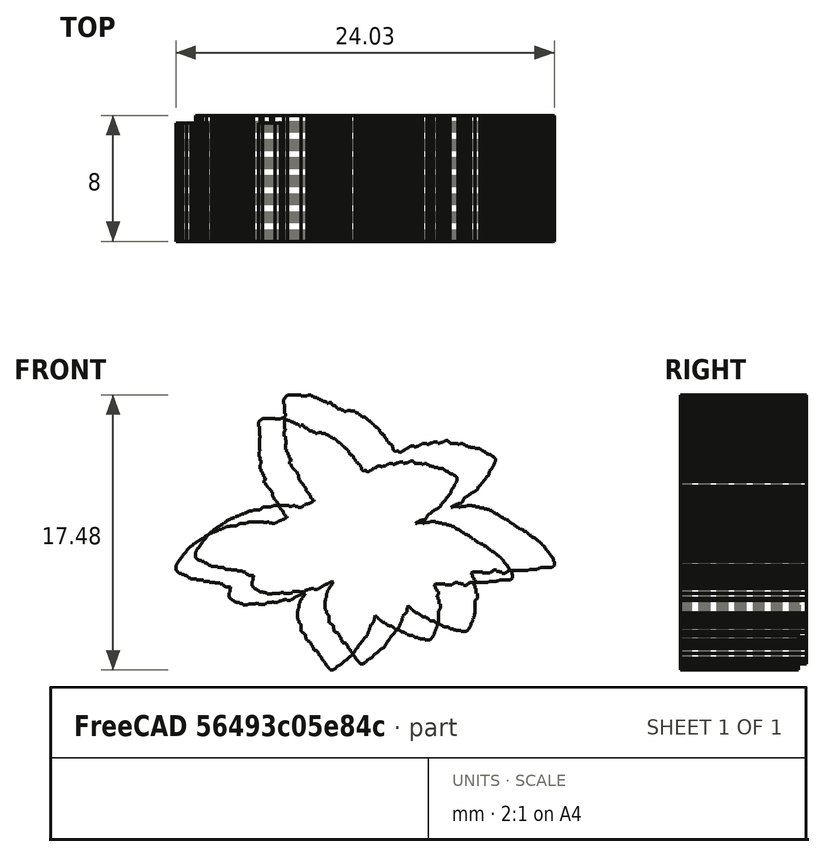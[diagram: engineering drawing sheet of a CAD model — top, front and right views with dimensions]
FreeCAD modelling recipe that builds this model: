
FCSTD DOCUMENT  (FreeCAD 0.20R29410 (Git))
Label: mintsLeafLogo_01_13_2023
License: All rights reserved
LicenseURL: http://en.wikipedia.org/wiki/All_rights_reserved
objects: Part::FeaturePython×2, Sketcher::SketchObject×1, Mesh::Feature×1, Part::Extrusion×1
note: 4 computed .brp shape members not serialized (recipe doc carries the construction recipe); baked Part::Feature solids carry a one-line shape summary decoded from their .brp

FEATURE [Sketcher::SketchObject] Sketch013
  FullyConstrained = false
  Placement = pos=(0,0,0) rot=(1,0,0;1.5708rad)
  sketch-geometry (884):
    g0: LineSegment StartX=35.7189 StartY=14.4677 StartZ=0 EndX=35.5415 EndY=14.2824 EndZ=0
    g1: LineSegment StartX=35.5415 StartY=14.2079 StartZ=0 EndX=35.4533 EndY=14.1342 EndZ=0
    g2: LineSegment StartX=35.4533 StartY=14.1342 StartZ=0 EndX=35.4583 EndY=14.0618 EndZ=0
    g3: LineSegment StartX=35.4583 StartY=14.0618 StartZ=0 EndX=35.3195 EndY=13.9216 EndZ=0
    g4: LineSegment StartX=35.3195 StartY=13.9216 StartZ=0 EndX=35.3195 EndY=13.853 EndZ=0
    g5: LineSegment StartX=35.3195 StartY=13.853 StartZ=0 EndX=35.248 EndY=13.7975 EndZ=0
    g6: LineSegment StartX=35.248 StartY=13.7975 StartZ=0 EndX=35.248 EndY=13.6573 EndZ=0
    g7: LineSegment StartX=35.248 StartY=13.6573 StartZ=0 EndX=35.1825 EndY=13.5912 EndZ=0
    g8: LineSegment StartX=35.1825 StartY=13.5912 StartZ=0 EndX=35.1825 EndY=13.2647 EndZ=0
    g9: LineSegment StartX=35.1825 StartY=13.2647 StartZ=0 EndX=35.0994 EndY=13.159 EndZ=0
    g10: LineSegment StartX=35.0994 StartY=13.159 StartZ=0 EndX=35.0994 EndY=13.0459 EndZ=0
    g11: LineSegment StartX=35.0994 StartY=13.0459 StartZ=0 EndX=35.0336 EndY=12.9565 EndZ=0
    g12: LineSegment StartX=35.0336 StartY=12.9565 StartZ=0 EndX=35.0336 EndY=12.3489 EndZ=0
    g13: LineSegment StartX=35.0336 StartY=12.3489 StartZ=0 EndX=35.1008 EndY=12.3489 EndZ=0
    g14: LineSegment StartX=35.1008 StartY=12.3489 StartZ=0 EndX=35.1008 EndY=12.2102 EndZ=0
    g15: LineSegment StartX=35.1008 StartY=12.2102 StartZ=0 EndX=35.1709 EndY=12.2072 EndZ=0
    g16: LineSegment StartX=35.1709 StartY=12.2072 StartZ=0 EndX=35.1709 EndY=11.9948 EndZ=0
    g17: LineSegment StartX=35.1709 StartY=11.9948 StartZ=0 EndX=35.2359 EndY=11.9948 EndZ=0
    g18: LineSegment StartX=35.2359 StartY=11.9948 StartZ=0 EndX=35.2359 EndY=11.9181 EndZ=0
    g19: LineSegment StartX=35.2359 StartY=11.9181 StartZ=0 EndX=35.3001 EndY=11.9181 EndZ=0
    g20: LineSegment StartX=35.3001 StartY=11.9181 StartZ=0 EndX=35.3001 EndY=11.8402 EndZ=0
    g21: LineSegment StartX=35.3001 StartY=11.8402 StartZ=0 EndX=35.3675 EndY=11.8402 EndZ=0
    g22: LineSegment StartX=35.3675 StartY=11.8402 StartZ=0 EndX=35.3675 EndY=11.2433 EndZ=0
    g23: LineSegment StartX=35.3675 StartY=11.2433 StartZ=0 EndX=35.435 EndY=11.2433 EndZ=0
    g24: LineSegment StartX=35.435 StartY=11.2433 StartZ=0 EndX=35.435 EndY=11.1727 EndZ=0
    g25: LineSegment StartX=35.435 StartY=11.1727 StartZ=0 EndX=35.5098 EndY=11.1727 EndZ=0
    g26: LineSegment StartX=35.5098 StartY=11.1727 StartZ=0 EndX=35.5098 EndY=11.1026 EndZ=0
    g27: LineSegment StartX=35.5098 StartY=11.1026 StartZ=0 EndX=35.6558 EndY=11.1026 EndZ=0
    g28: LineSegment StartX=35.6558 StartY=11.1026 StartZ=0 EndX=35.6558 EndY=11.0252 EndZ=0
    g29: LineSegment StartX=35.6558 StartY=11.0252 StartZ=0 EndX=35.7128 EndY=11.0252 EndZ=0
    g30: LineSegment StartX=35.7128 StartY=11.0252 StartZ=0 EndX=35.7128 EndY=10.7682 EndZ=0
    g31: LineSegment StartX=35.7128 StartY=10.7682 StartZ=0 EndX=35.7756 EndY=10.7681 EndZ=0
    g32: LineSegment StartX=35.7756 StartY=10.7681 StartZ=0 EndX=35.7756 EndY=10.5644 EndZ=0
    g33: LineSegment StartX=35.7756 StartY=10.5644 StartZ=0 EndX=35.846 EndY=10.5644 EndZ=0
    g34: LineSegment StartX=35.846 StartY=10.5644 StartZ=0 EndX=35.846 EndY=10.4767 EndZ=0
    g35: LineSegment StartX=35.846 StartY=10.4767 StartZ=0 EndX=35.988 EndY=10.4767 EndZ=0
    g36: LineSegment StartX=35.988 StartY=10.4767 StartZ=0 EndX=35.988 EndY=10.4228 EndZ=0
    g37: LineSegment StartX=35.988 StartY=10.4228 StartZ=0 EndX=36.1201 EndY=10.4228 EndZ=0
    g38: LineSegment StartX=36.1201 StartY=10.4228 StartZ=0 EndX=36.1201 EndY=10.2907 EndZ=0
    g39: LineSegment StartX=36.1201 StartY=10.2907 StartZ=0 EndX=36.1926 EndY=10.2907 EndZ=0
    g40: LineSegment StartX=36.1926 StartY=10.2907 StartZ=0 EndX=36.1926 EndY=10.1585 EndZ=0
    g41: LineSegment StartX=36.1926 StartY=10.1585 StartZ=0 EndX=36.2533 EndY=10.1585 EndZ=0
    g42: LineSegment StartX=36.2533 StartY=10.1585 StartZ=0 EndX=36.2533 EndY=10.0897 EndZ=0
    g43: LineSegment StartX=36.2533 StartY=10.0897 StartZ=0 EndX=36.3179 EndY=10.0897 EndZ=0
    g44: LineSegment StartX=36.3179 StartY=10.0897 StartZ=0 EndX=36.3179 EndY=9.8871 EndZ=0
    g45: LineSegment StartX=36.3179 StartY=9.8871 StartZ=0 EndX=36.3888 EndY=9.8871 EndZ=0
    g46: LineSegment StartX=36.3888 StartY=9.8871 StartZ=0 EndX=36.3888 EndY=9.73503 EndZ=0
    g47: LineSegment StartX=36.3888 StartY=9.73503 StartZ=0 EndX=36.4516 EndY=9.73503 EndZ=0
    g48: LineSegment StartX=36.4516 StartY=9.73503 StartZ=0 EndX=36.4516 EndY=9.65617 EndZ=0
    g49: LineSegment StartX=36.4516 StartY=9.65617 StartZ=0 EndX=36.6707 EndY=9.65617 EndZ=0
    g50: LineSegment StartX=36.6707 StartY=9.65617 StartZ=0 EndX=36.6707 EndY=9.58899 EndZ=0
    g51: LineSegment StartX=36.6707 StartY=9.58899 StartZ=0 EndX=36.7335 EndY=9.58899 EndZ=0
    g52: LineSegment StartX=36.7335 StartY=9.58899 StartZ=0 EndX=36.7335 EndY=9.51158 EndZ=0
    g53: LineSegment StartX=36.7335 StartY=9.51158 StartZ=0 EndX=36.7948 EndY=9.51158 EndZ=0
    g54: LineSegment StartX=36.7948 StartY=9.51158 StartZ=0 EndX=36.7948 EndY=9.40351 EndZ=0
    g55: LineSegment StartX=36.7948 StartY=9.40351 StartZ=0 EndX=36.8664 EndY=9.40351 EndZ=0
    g56: LineSegment StartX=36.8664 StartY=9.40351 StartZ=0 EndX=36.8664 EndY=9.2487 EndZ=0
    g57: LineSegment StartX=36.8664 StartY=9.2487 StartZ=0 EndX=36.9292 EndY=9.2487 EndZ=0
    g58: LineSegment StartX=36.9292 StartY=9.2487 StartZ=0 EndX=36.9292 EndY=9.18298 EndZ=0
    g59: LineSegment StartX=36.9292 StartY=9.18298 StartZ=0 EndX=37.0036 EndY=9.18298 EndZ=0
    g60: LineSegment StartX=37.0036 StartY=9.18298 StartZ=0 EndX=37.0036 EndY=9.12121 EndZ=0
    g61: LineSegment StartX=37.0036 StartY=9.12121 StartZ=0 EndX=37.066 EndY=9.12121 EndZ=0
    g62: LineSegment StartX=37.066 StartY=9.12121 StartZ=0 EndX=37.066 EndY=8.98122 EndZ=0
    g63: LineSegment StartX=37.066 StartY=8.98122 StartZ=0 EndX=37.1365 EndY=8.98122 EndZ=0
    g64: LineSegment StartX=37.1365 StartY=8.98122 StartZ=0 EndX=37.1365 EndY=8.85617 EndZ=0
    g65: LineSegment StartX=37.1365 StartY=8.85617 StartZ=0 EndX=37.2117 EndY=8.85617 EndZ=0
    g66: LineSegment StartX=37.2117 StartY=8.85617 StartZ=0 EndX=37.2117 EndY=8.77808 EndZ=0
    g67: LineSegment StartX=37.2117 StartY=8.77808 StartZ=0 EndX=37.276 EndY=8.7779 EndZ=0
    g68: LineSegment StartX=37.276 StartY=8.7779 StartZ=0 EndX=37.276 EndY=8.70839 EndZ=0
    g69: LineSegment StartX=37.276 StartY=8.70839 StartZ=0 EndX=37.3475 EndY=8.70839 EndZ=0
    g70: LineSegment StartX=37.3475 StartY=8.70839 StartZ=0 EndX=37.3475 EndY=8.58602 EndZ=0
    g71: LineSegment StartX=37.3475 StartY=8.58602 StartZ=0 EndX=37.4111 EndY=8.58602 EndZ=0
    g72: LineSegment StartX=37.4111 StartY=8.58602 StartZ=0 EndX=37.4111 EndY=8.50272 EndZ=0
    g73: LineSegment StartX=37.4111 StartY=8.50272 StartZ=0 EndX=37.4778 EndY=8.50272 EndZ=0
    g74: LineSegment StartX=37.4778 StartY=8.50272 StartZ=0 EndX=37.4778 EndY=8.37852 EndZ=0
    g75: LineSegment StartX=37.4778 StartY=8.37852 StartZ=0 EndX=37.55 EndY=8.37852 EndZ=0
    g76: LineSegment StartX=37.55 StartY=8.37852 StartZ=0 EndX=37.55 EndY=8.29594 EndZ=0
    g77: LineSegment StartX=37.55 StartY=8.29594 StartZ=0 EndX=37.6238 EndY=8.29594 EndZ=0
    g78: LineSegment StartX=37.6238 StartY=8.29594 StartZ=0 EndX=37.6238 EndY=8.20831 EndZ=0
    g79: LineSegment StartX=37.6238 StartY=8.20831 StartZ=0 EndX=37.6953 EndY=8.21123 EndZ=0
    g80: LineSegment StartX=37.6953 StartY=8.21123 StartZ=0 EndX=37.6953 EndY=8.14022 EndZ=0
    g81: LineSegment StartX=37.6953 StartY=8.14022 StartZ=0 EndX=37.7536 EndY=8.14414 EndZ=0
    g82: LineSegment StartX=37.7536 StartY=8.14414 StartZ=0 EndX=37.7574 EndY=8.06459 EndZ=0
    g83: LineSegment StartX=37.7574 StartY=8.06459 StartZ=0 EndX=37.8181 EndY=8.06459 EndZ=0
    g84: LineSegment StartX=37.8181 StartY=8.06459 StartZ=0 EndX=37.8216 EndY=7.98967 EndZ=0
    g85: LineSegment StartX=37.8216 StartY=7.98967 StartZ=0 EndX=38.1025 EndY=7.98967 EndZ=0
    g86: LineSegment StartX=38.1025 StartY=7.98967 StartZ=0 EndX=38.1917 EndY=8.08042 EndZ=0
    g87: LineSegment StartX=38.1917 StartY=8.08042 StartZ=0 EndX=38.2417 EndY=8.08577 EndZ=0
    g88: LineSegment StartX=38.2417 StartY=8.08577 StartZ=0 EndX=38.4557 EndY=8.32302 EndZ=0
    g89: LineSegment StartX=38.4557 StartY=8.32302 StartZ=0 EndX=38.5235 EndY=8.32302 EndZ=0
    g90: LineSegment StartX=38.5235 StartY=8.32302 StartZ=0 EndX=38.5887 EndY=8.40314 EndZ=0
    g91: LineSegment StartX=38.5887 StartY=8.40314 StartZ=0 EndX=38.6773 EndY=8.40314 EndZ=0
    g92: LineSegment StartX=38.6773 StartY=8.40314 StartZ=0 EndX=39.0643 EndY=8.80818 EndZ=0
    g93: LineSegment StartX=39.0643 StartY=8.80818 StartZ=0 EndX=39.152 EndY=8.80818 EndZ=0
    g94: LineSegment StartX=39.152 StartY=8.80818 StartZ=0 EndX=39.5355 EndY=9.19803 EndZ=0
    g95: LineSegment StartX=39.5355 StartY=9.19803 StartZ=0 EndX=39.6318 EndY=9.19803 EndZ=0
    g96: LineSegment StartX=39.6318 StartY=9.19803 StartZ=0 EndX=39.792 EndY=9.38195 EndZ=0
    g97: LineSegment StartX=39.792 StartY=9.38195 StartZ=0 EndX=39.7884 EndY=9.45608 EndZ=0
    g98: LineSegment StartX=39.7884 StartY=9.45608 StartZ=0 EndX=39.9772 EndY=9.63446 EndZ=0
    g99: LineSegment StartX=39.9772 StartY=9.63446 StartZ=0 EndX=39.9772 EndY=9.72533 EndZ=0
    g100: LineSegment StartX=39.9772 StartY=9.72533 StartZ=0 EndX=40.1697 EndY=9.91904 EndZ=0
    g101: LineSegment StartX=40.1697 StartY=9.91904 StartZ=0 EndX=40.1746 EndY=9.99558 EndZ=0
    g102: LineSegment StartX=40.1746 StartY=9.99558 StartZ=0 EndX=40.2388 EndY=10.0603 EndZ=0
    g103: LineSegment StartX=40.2388 StartY=10.0603 StartZ=0 EndX=40.2423 EndY=10.1261 EndZ=0
    g104: LineSegment StartX=40.2423 StartY=10.1261 StartZ=0 EndX=40.5948 EndY=10.4793 EndZ=0
    g105: LineSegment StartX=40.5948 StartY=10.4793 StartZ=0 EndX=40.5948 EndY=10.5499 EndZ=0
    g106: LineSegment StartX=40.5948 StartY=10.5499 StartZ=0 EndX=40.6701 EndY=10.618 EndZ=0
    g107: LineSegment StartX=40.6701 StartY=10.618 StartZ=0 EndX=40.6581 EndY=10.6527 EndZ=0
    g108: LineSegment StartX=40.6581 StartY=10.6527 StartZ=0 EndX=40.6988 EndY=10.6527 EndZ=0
    g109: LineSegment StartX=40.6988 StartY=10.6527 StartZ=0 EndX=40.9317 EndY=10.8877 EndZ=0
    g110: LineSegment StartX=40.9317 StartY=10.8877 StartZ=0 EndX=40.9317 EndY=10.9592 EndZ=0
    g111: LineSegment StartX=40.9317 StartY=10.9592 StartZ=0 EndX=41.0136 EndY=11.0405 EndZ=0
    g112: LineSegment StartX=41.0136 StartY=11.0405 StartZ=0 EndX=41.0068 EndY=11.1648 EndZ=0
    g113: LineSegment StartX=41.0068 StartY=11.1648 StartZ=0 EndX=41.0763 EndY=11.2275 EndZ=0
    g114: LineSegment StartX=41.0763 StartY=11.2275 StartZ=0 EndX=41.0723 EndY=11.2979 EndZ=0
    g115: LineSegment StartX=41.0723 StartY=11.2979 StartZ=0 EndX=41.15 EndY=11.3821 EndZ=0
    g116: LineSegment StartX=41.15 StartY=11.3821 StartZ=0 EndX=41.15 EndY=11.5724 EndZ=0
    g117: LineSegment StartX=41.15 StartY=11.5724 StartZ=0 EndX=41.2317 EndY=11.6351 EndZ=0
    g118: LineSegment StartX=41.2317 StartY=11.6351 StartZ=0 EndX=41.2155 EndY=11.7717 EndZ=0
    g119: LineSegment StartX=41.2155 StartY=11.7717 StartZ=0 EndX=41.2837 EndY=11.8432 EndZ=0
    g120: LineSegment StartX=41.2837 StartY=11.8432 StartZ=0 EndX=41.2786 EndY=11.8698 EndZ=0
    g121: LineSegment StartX=41.2786 StartY=11.8698 StartZ=0 EndX=41.3138 EndY=11.8698 EndZ=0
    g122: LineSegment StartX=41.3138 StartY=11.8698 StartZ=0 EndX=41.5455 EndY=12.1045 EndZ=0
    g123: LineSegment StartX=41.5455 StartY=12.1045 StartZ=0 EndX=41.5618 EndY=12.4305 EndZ=0
    g124: LineSegment StartX=41.5618 StartY=12.4305 StartZ=0 EndX=41.6277 EndY=12.505 EndZ=0
    g125: LineSegment StartX=41.6277 StartY=12.505 StartZ=0 EndX=41.6277 EndY=12.6108 EndZ=0
    g126: LineSegment StartX=41.6277 StartY=12.6108 StartZ=0 EndX=41.692 EndY=12.5393 EndZ=0
    g127: LineSegment StartX=41.692 StartY=12.5393 StartZ=0 EndX=41.7679 EndY=12.5393 EndZ=0
    g128: LineSegment StartX=41.7679 StartY=12.5393 StartZ=0 EndX=41.7679 EndY=12.4516 EndZ=0
    g129: LineSegment StartX=41.7679 StartY=12.4516 StartZ=0 EndX=41.8336 EndY=12.4546 EndZ=0
    g130: LineSegment StartX=41.8336 StartY=12.4546 StartZ=0 EndX=41.8336 EndY=12.3903 EndZ=0
    g131: LineSegment StartX=41.8336 StartY=12.3903 StartZ=0 EndX=41.8935 EndY=12.3903 EndZ=0
    g132: LineSegment StartX=41.8935 StartY=12.3903 StartZ=0 EndX=41.8935 EndY=12.3173 EndZ=0
    g133: LineSegment StartX=41.8935 StartY=12.3173 StartZ=0 EndX=41.9592 EndY=12.3217 EndZ=0
    g134: LineSegment StartX=41.9592 StartY=12.3217 StartZ=0 EndX=41.9651 EndY=12.2501 EndZ=0
    g135: LineSegment StartX=41.9651 StartY=12.2501 StartZ=0 EndX=42.0235 EndY=12.2559 EndZ=0
    g136: LineSegment StartX=42.0235 StartY=12.2559 StartZ=0 EndX=42.0264 EndY=12.1829 EndZ=0
    g137: LineSegment StartX=42.0264 StartY=12.1829 StartZ=0 EndX=42.1067 EndY=12.1888 EndZ=0
    g138: LineSegment StartX=42.1067 StartY=12.1888 StartZ=0 EndX=42.1067 EndY=12.1143 EndZ=0
    g139: LineSegment StartX=42.1067 StartY=12.1143 StartZ=0 EndX=42.2426 EndY=12.1216 EndZ=0
    g140: LineSegment StartX=42.2426 StartY=12.1216 StartZ=0 EndX=42.2426 EndY=12.0413 EndZ=0
    g141: LineSegment StartX=42.2426 StartY=12.0413 StartZ=0 EndX=42.4427 EndY=12.0413 EndZ=0
    g142: LineSegment StartX=42.4427 StartY=12.0413 StartZ=0 EndX=42.45 EndY=11.9566 EndZ=0
    g143: LineSegment StartX=42.45 StartY=11.9566 StartZ=0 EndX=42.523 EndY=11.9639 EndZ=0
    g144: LineSegment StartX=42.523 StartY=11.9639 StartZ=0 EndX=42.5274 EndY=11.8952 EndZ=0
    g145: LineSegment StartX=42.5274 StartY=11.8952 StartZ=0 EndX=42.5931 EndY=11.9011 EndZ=0
    g146: LineSegment StartX=42.5931 StartY=11.9011 StartZ=0 EndX=42.5931 EndY=11.847 EndZ=0
    g147: LineSegment StartX=42.5931 StartY=11.847 StartZ=0 EndX=42.6457 EndY=11.8499 EndZ=0
    g148: LineSegment StartX=42.6457 StartY=11.8499 StartZ=0 EndX=42.6457 EndY=11.7886 EndZ=0
    g149: LineSegment StartX=42.6457 StartY=11.7886 StartZ=0 EndX=42.7844 EndY=11.7886 EndZ=0
    g150: LineSegment StartX=42.7844 StartY=11.7886 StartZ=0 EndX=42.7844 EndY=11.7131 EndZ=0
    g151: LineSegment StartX=42.7844 StartY=11.7131 StartZ=0 EndX=43.0642 EndY=11.7131 EndZ=0
    g152: LineSegment StartX=43.0642 StartY=11.7131 StartZ=0 EndX=43.0642 EndY=11.6357 EndZ=0
    g153: LineSegment StartX=43.0642 StartY=11.6357 StartZ=0 EndX=43.1985 EndY=11.6357 EndZ=0
    g154: LineSegment StartX=43.1985 StartY=11.6357 StartZ=0 EndX=43.1985 EndY=11.5714 EndZ=0
    g155: LineSegment StartX=43.1985 StartY=11.5714 StartZ=0 EndX=43.2613 EndY=11.5714 EndZ=0
    g156: LineSegment StartX=43.2613 StartY=11.5714 StartZ=0 EndX=43.2613 EndY=11.5086 EndZ=0
    g157: LineSegment StartX=43.2613 StartY=11.5086 StartZ=0 EndX=43.3285 EndY=11.5086 EndZ=0
    g158: LineSegment StartX=43.3285 StartY=11.5086 StartZ=0 EndX=43.3285 EndY=11.4327 EndZ=0
    g159: LineSegment StartX=43.3285 StartY=11.4327 StartZ=0 EndX=43.3913 EndY=11.4371 EndZ=0
    g160: LineSegment StartX=43.3913 StartY=11.4371 StartZ=0 EndX=43.3932 EndY=11.3717 EndZ=0
    g161: LineSegment StartX=43.3932 StartY=11.3717 StartZ=0 EndX=43.7436 EndY=11.3717 EndZ=0
    g162: LineSegment StartX=43.7436 StartY=11.3717 StartZ=0 EndX=43.7436 EndY=11.3021 EndZ=0
    g163: LineSegment StartX=43.7436 StartY=11.3021 StartZ=0 EndX=43.8098 EndY=11.3021 EndZ=0
    g164: LineSegment StartX=43.8098 StartY=11.3021 StartZ=0 EndX=43.8134 EndY=11.2285 EndZ=0
    g165: LineSegment StartX=43.8134 StartY=11.2285 StartZ=0 EndX=44.0238 EndY=11.2285 EndZ=0
    g166: LineSegment StartX=44.0238 StartY=11.2285 StartZ=0 EndX=44.0238 EndY=11.1603 EndZ=0
    g167: LineSegment StartX=44.0238 StartY=11.1603 StartZ=0 EndX=44.1542 EndY=11.1603 EndZ=0
    g168: LineSegment StartX=44.1542 StartY=11.1603 StartZ=0 EndX=44.1506 EndY=11.0922 EndZ=0
    g169: LineSegment StartX=44.1506 StartY=11.0922 StartZ=0 EndX=44.2845 EndY=11.1005 EndZ=0
    g170: LineSegment StartX=44.2845 StartY=11.1005 StartZ=0 EndX=44.2845 EndY=11.0276 EndZ=0
    g171: LineSegment StartX=44.2845 StartY=11.0276 StartZ=0 EndX=44.3538 EndY=11.0312 EndZ=0
    g172: LineSegment StartX=44.3538 StartY=11.0312 StartZ=0 EndX=44.3538 EndY=10.9534 EndZ=0
    g173: LineSegment StartX=44.3538 StartY=10.9534 StartZ=0 EndX=44.4925 EndY=10.9534 EndZ=0
    g174: LineSegment StartX=44.4925 StartY=10.9534 StartZ=0 EndX=44.4925 EndY=10.9066 EndZ=0
    g175: LineSegment StartX=44.4925 StartY=10.9066 StartZ=0 EndX=44.8405 EndY=10.9066 EndZ=0
    g176: LineSegment StartX=44.8405 StartY=10.9066 StartZ=0 EndX=44.8405 EndY=10.8227 EndZ=0
    g177: LineSegment StartX=44.8405 StartY=10.8227 StartZ=0 EndX=44.9671 EndY=10.8245 EndZ=0
    g178: LineSegment StartX=44.9671 StartY=10.8245 StartZ=0 EndX=44.9671 EndY=10.7496 EndZ=0
    g179: LineSegment StartX=44.9671 StartY=10.7496 StartZ=0 EndX=45.2382 EndY=10.7496 EndZ=0
    g180: LineSegment StartX=45.2382 StartY=10.7496 StartZ=0 EndX=45.2382 EndY=10.6783 EndZ=0
    g181: LineSegment StartX=45.2382 StartY=10.6783 StartZ=0 EndX=45.438 EndY=10.6783 EndZ=0
    g182: LineSegment StartX=45.438 StartY=10.6783 StartZ=0 EndX=45.438 EndY=10.6176 EndZ=0
    g183: LineSegment StartX=45.438 StartY=10.6176 StartZ=0 EndX=45.8572 EndY=10.6176 EndZ=0
    g184: LineSegment StartX=45.8572 StartY=10.6176 StartZ=0 EndX=45.8572 EndY=10.548 EndZ=0
    g185: LineSegment StartX=45.8572 StartY=10.548 StartZ=0 EndX=46.2711 EndY=10.548 EndZ=0
    g186: LineSegment StartX=46.2711 StartY=10.548 StartZ=0 EndX=46.5712 EndY=10.876 EndZ=0
    g187: LineSegment StartX=46.5712 StartY=10.876 StartZ=0 EndX=46.568 EndY=10.9537 EndZ=0
    g188: LineSegment StartX=46.568 StartY=10.9537 StartZ=0 EndX=46.6513 EndY=11.0387 EndZ=0
    g189: LineSegment StartX=46.6513 StartY=11.0387 StartZ=0 EndX=46.6513 EndY=11.2162 EndZ=0
    g190: LineSegment StartX=46.6513 StartY=11.2162 StartZ=0 EndX=46.7535 EndY=11.317 EndZ=0
    g191: LineSegment StartX=46.7535 StartY=11.317 StartZ=0 EndX=46.7462 EndY=11.4353 EndZ=0
    g192: LineSegment StartX=46.7462 StartY=11.4353 StartZ=0 EndX=46.8178 EndY=11.5141 EndZ=0
    g193: LineSegment StartX=46.8178 StartY=11.5141 StartZ=0 EndX=46.8081 EndY=11.636 EndZ=0
    g194: LineSegment StartX=46.8081 StartY=11.636 StartZ=0 EndX=46.8919 EndY=11.7287 EndZ=0
    g195: LineSegment StartX=46.8919 StartY=11.7287 StartZ=0 EndX=46.8919 EndY=11.9142 EndZ=0
    g196: LineSegment StartX=46.8919 StartY=11.9142 StartZ=0 EndX=46.9704 EndY=12.0106 EndZ=0
    g197: LineSegment StartX=46.9704 StartY=12.0106 StartZ=0 EndX=46.9704 EndY=13.0147 EndZ=0
    g198: LineSegment StartX=46.9704 StartY=13.0147 StartZ=0 EndX=47.1435 EndY=13.1957 EndZ=0
    g199: LineSegment StartX=47.1435 StartY=13.1957 StartZ=0 EndX=47.1435 EndY=13.5812 EndZ=0
    g200: LineSegment StartX=47.1435 StartY=13.5812 StartZ=0 EndX=47.0232 EndY=13.5812 EndZ=0
    g201: LineSegment StartX=47.0232 StartY=13.5812 StartZ=0 EndX=47.0232 EndY=13.968 EndZ=0
    g202: LineSegment StartX=47.0232 StartY=13.968 StartZ=0 EndX=46.9387 EndY=13.981 EndZ=0
    g203: LineSegment StartX=46.9387 StartY=13.981 StartZ=0 EndX=46.9387 EndY=14.1923 EndZ=0
    g204: LineSegment StartX=46.9387 StartY=14.1923 StartZ=0 EndX=46.8607 EndY=14.189 EndZ=0
    g205: LineSegment StartX=46.8607 StartY=14.189 StartZ=0 EndX=46.8607 EndY=14.2768 EndZ=0
    g206: LineSegment StartX=46.8607 StartY=14.2768 StartZ=0 EndX=46.9745 EndY=14.4003 EndZ=0
    g207: LineSegment StartX=46.9745 StartY=14.4003 StartZ=0 EndX=46.9842 EndY=14.6473 EndZ=0
    g208: LineSegment StartX=46.9842 StartY=14.6473 StartZ=0 EndX=46.8672 EndY=14.6603 EndZ=0
    g209: LineSegment StartX=46.8672 StartY=14.6603 StartZ=0 EndX=46.8672 EndY=14.8066 EndZ=0
    g210: LineSegment StartX=46.8672 StartY=14.8066 StartZ=0 EndX=46.799 EndY=14.8131 EndZ=0
    g211: LineSegment StartX=46.799 StartY=14.8131 StartZ=0 EndX=46.7957 EndY=14.8846 EndZ=0
    g212: LineSegment StartX=46.7957 StartY=14.8846 StartZ=0 EndX=46.7372 EndY=14.8911 EndZ=0
    g213: LineSegment StartX=46.7372 StartY=14.8911 StartZ=0 EndX=46.7502 EndY=15.0699 EndZ=0
    g214: LineSegment StartX=46.7502 StartY=15.0699 StartZ=0 EndX=46.6592 EndY=15.0764 EndZ=0
    g215: LineSegment StartX=46.6592 StartY=15.0764 StartZ=0 EndX=46.6592 EndY=15.2096 EndZ=0
    g216: LineSegment StartX=46.6592 StartY=15.2096 StartZ=0 EndX=46.7535 EndY=15.2811 EndZ=0
    g217: LineSegment StartX=46.7535 StartY=15.2811 StartZ=0 EndX=47.5498 EndY=15.2811 EndZ=0
    g218: LineSegment StartX=47.5498 StartY=15.2811 StartZ=0 EndX=47.5498 EndY=15.2015 EndZ=0
    g219: LineSegment StartX=47.5498 StartY=15.2015 StartZ=0 EndX=48.1326 EndY=15.2015 EndZ=0
    g220: LineSegment StartX=48.1326 StartY=15.2015 StartZ=0 EndX=48.1915 EndY=15.2887 EndZ=0
    g221: LineSegment StartX=48.1915 StartY=15.2887 StartZ=0 EndX=48.2811 EndY=15.2887 EndZ=0
    g222: LineSegment StartX=48.2811 StartY=15.2887 StartZ=0 EndX=48.4046 EndY=15.4194 EndZ=0
    g223: LineSegment StartX=48.4046 StartY=15.4194 StartZ=0 EndX=48.6512 EndY=15.4194 EndZ=0
    g224: LineSegment StartX=48.6512 StartY=15.4194 StartZ=0 EndX=48.6512 EndY=15.3322 EndZ=0
    g225: LineSegment StartX=48.6512 StartY=15.3322 StartZ=0 EndX=48.9084 EndY=15.3322 EndZ=0
    g226: LineSegment StartX=48.9084 StartY=15.3322 StartZ=0 EndX=48.9084 EndY=15.2647 EndZ=0
    g227: LineSegment StartX=48.9084 StartY=15.2647 StartZ=0 EndX=49.1131 EndY=15.2647 EndZ=0
    g228: LineSegment StartX=49.1131 StartY=15.2647 StartZ=0 EndX=49.1131 EndY=15.171 EndZ=0
    g229: LineSegment StartX=49.1131 StartY=15.171 StartZ=0 EndX=49.344 EndY=15.171 EndZ=0
    g230: LineSegment StartX=49.344 StartY=15.171 StartZ=0 EndX=49.4317 EndY=15.2779 EndZ=0
    g231: LineSegment StartX=49.4317 StartY=15.2779 StartZ=0 EndX=49.513 EndY=15.2714 EndZ=0
    g232: LineSegment StartX=49.513 StartY=15.2714 StartZ=0 EndX=49.6365 EndY=15.4177 EndZ=0
    g233: LineSegment StartX=49.6365 StartY=15.4177 StartZ=0 EndX=51.1609 EndY=15.4177 EndZ=0
    g234: LineSegment StartX=51.1609 StartY=15.4177 StartZ=0 EndX=51.2713 EndY=15.4747 EndZ=0
    g235: LineSegment StartX=51.2713 StartY=15.4747 StartZ=0 EndX=51.8707 EndY=15.4747 EndZ=0
    g236: LineSegment StartX=51.8707 StartY=15.4747 StartZ=0 EndX=51.9501 EndY=15.5501 EndZ=0
    g237: LineSegment StartX=51.9501 StartY=15.5501 StartZ=0 EndX=52.0613 EndY=15.5501 EndZ=0
    g238: LineSegment StartX=52.0613 StartY=15.5501 StartZ=0 EndX=52.1566 EndY=15.6335 EndZ=0
    g239: LineSegment StartX=52.1566 StartY=15.6335 StartZ=0 EndX=53.0776 EndY=15.6335 EndZ=0
    g240: LineSegment StartX=53.0776 StartY=15.6335 StartZ=0 EndX=53.2557 EndY=15.8082 EndZ=0
    g241: LineSegment StartX=53.2557 StartY=15.8082 StartZ=0 EndX=53.2557 EndY=16.103 EndZ=0
    g242: LineSegment StartX=53.2557 StartY=16.103 StartZ=0 EndX=53.1958 EndY=16.103 EndZ=0
    g243: LineSegment StartX=53.1958 StartY=16.103 StartZ=0 EndX=53.1958 EndY=16.3046 EndZ=0
    g244: LineSegment StartX=53.1958 StartY=16.3046 StartZ=0 EndX=53.1301 EndY=16.3017 EndZ=0
    g245: LineSegment StartX=53.1301 StartY=16.3017 StartZ=0 EndX=53.1301 EndY=16.4404 EndZ=0
    g246: LineSegment StartX=53.1301 StartY=16.4404 StartZ=0 EndX=53.0594 EndY=16.4404 EndZ=0
    g247: LineSegment StartX=53.0594 StartY=16.4404 StartZ=0 EndX=53.0558 EndY=16.5171 EndZ=0
    g248: LineSegment StartX=53.0558 StartY=16.5171 StartZ=0 EndX=52.9773 EndY=16.5171 EndZ=0
    g249: LineSegment StartX=52.9773 StartY=16.5171 StartZ=0 EndX=52.9773 EndY=16.6455 EndZ=0
    g250: LineSegment StartX=52.9773 StartY=16.6455 StartZ=0 EndX=52.9219 EndY=16.6452 EndZ=0
    g251: LineSegment StartX=52.9219 StartY=16.6452 StartZ=0 EndX=52.9219 EndY=16.7146 EndZ=0
    g252: LineSegment StartX=52.9219 StartY=16.7146 StartZ=0 EndX=52.8549 EndY=16.7146 EndZ=0
    g253: LineSegment StartX=52.8549 StartY=16.7146 StartZ=0 EndX=52.8535 EndY=16.7863 EndZ=0
    g254: LineSegment StartX=52.8535 StartY=16.7863 StartZ=0 EndX=52.7868 EndY=16.7863 EndZ=0
    g255: LineSegment StartX=52.7868 StartY=16.7863 StartZ=0 EndX=52.7868 EndY=16.9211 EndZ=0
    g256: LineSegment StartX=52.7868 StartY=16.9211 StartZ=0 EndX=52.715 EndY=16.9211 EndZ=0
    g257: LineSegment StartX=52.715 StartY=16.9211 StartZ=0 EndX=52.715 EndY=16.98 EndZ=0
    g258: LineSegment StartX=52.715 StartY=16.98 StartZ=0 EndX=52.6457 EndY=16.98 EndZ=0
    g259: LineSegment StartX=52.6457 StartY=16.98 StartZ=0 EndX=52.6457 EndY=17.0366 EndZ=0
    g260: LineSegment StartX=52.6457 StartY=17.0366 StartZ=0 EndX=52.5763 EndY=17.0366 EndZ=0
    g261: LineSegment StartX=52.5763 StartY=17.0366 StartZ=0 EndX=52.5763 EndY=17.128 EndZ=0
    g262: LineSegment StartX=52.5763 StartY=17.128 StartZ=0 EndX=52.5147 EndY=17.128 EndZ=0
    g263: LineSegment StartX=52.5147 StartY=17.128 StartZ=0 EndX=52.5147 EndY=17.2695 EndZ=0
    g264: LineSegment StartX=52.5147 StartY=17.2695 StartZ=0 EndX=52.4502 EndY=17.2647 EndZ=0
    g265: LineSegment StartX=52.4502 StartY=17.2647 StartZ=0 EndX=52.4454 EndY=17.336 EndZ=0
    g266: LineSegment StartX=52.4454 StartY=17.336 StartZ=0 EndX=52.3797 EndY=17.3384 EndZ=0
    g267: LineSegment StartX=52.3797 StartY=17.3384 StartZ=0 EndX=52.3829 EndY=17.4058 EndZ=0
    g268: LineSegment StartX=52.3829 StartY=17.4058 StartZ=0 EndX=52.318 EndY=17.4026 EndZ=0
    g269: LineSegment StartX=52.318 StartY=17.4026 StartZ=0 EndX=52.318 EndY=17.4715 EndZ=0
    g270: LineSegment StartX=52.318 StartY=17.4715 StartZ=0 EndX=52.2451 EndY=17.4715 EndZ=0
    g271: LineSegment StartX=52.2451 StartY=17.4715 StartZ=0 EndX=52.2451 EndY=17.5364 EndZ=0
    g272: LineSegment StartX=52.2451 StartY=17.5364 StartZ=0 EndX=52.1833 EndY=17.5388 EndZ=0
    g273: LineSegment StartX=52.1833 StartY=17.5388 StartZ=0 EndX=52.1833 EndY=17.6077 EndZ=0
    g274: LineSegment StartX=52.1833 StartY=17.6077 StartZ=0 EndX=52.1144 EndY=17.6077 EndZ=0
    g275: LineSegment StartX=52.1144 StartY=17.6077 StartZ=0 EndX=52.1144 EndY=17.6741 EndZ=0
    g276: LineSegment StartX=52.1144 StartY=17.6741 StartZ=0 EndX=52.0495 EndY=17.6741 EndZ=0
    g277: LineSegment StartX=52.0495 StartY=17.6741 StartZ=0 EndX=52.0495 EndY=17.7495 EndZ=0
    g278: LineSegment StartX=52.0495 StartY=17.7495 StartZ=0 EndX=51.9017 EndY=17.7495 EndZ=0
    g279: LineSegment StartX=51.9017 StartY=17.7495 StartZ=0 EndX=51.9017 EndY=17.8092 EndZ=0
    g280: LineSegment StartX=51.9017 StartY=17.8092 StartZ=0 EndX=51.8351 EndY=17.8092 EndZ=0
    g281: LineSegment StartX=51.8351 StartY=17.8092 StartZ=0 EndX=51.8351 EndY=17.8911 EndZ=0
    g282: LineSegment StartX=51.8351 StartY=17.8911 StartZ=0 EndX=51.7639 EndY=17.8911 EndZ=0
    g283: LineSegment StartX=51.7639 StartY=17.8911 StartZ=0 EndX=51.7639 EndY=17.9626 EndZ=0
    g284: LineSegment StartX=51.7639 StartY=17.9626 StartZ=0 EndX=51.6325 EndY=17.9626 EndZ=0
    g285: LineSegment StartX=51.6325 StartY=17.9626 StartZ=0 EndX=51.6325 EndY=18.0284 EndZ=0
    g286: LineSegment StartX=51.6325 StartY=18.0284 StartZ=0 EndX=51.485 EndY=18.0284 EndZ=0
    g287: LineSegment StartX=51.485 StartY=18.0284 StartZ=0 EndX=51.485 EndY=18.0711 EndZ=0
    g288: LineSegment StartX=51.485 StartY=18.0711 StartZ=0 EndX=51.4163 EndY=18.0711 EndZ=0
    g289: LineSegment StartX=51.4163 StartY=18.0711 StartZ=0 EndX=51.4163 EndY=18.1587 EndZ=0
    g290: LineSegment StartX=51.4163 StartY=18.1587 StartZ=0 EndX=51.2878 EndY=18.1587 EndZ=0
    g291: LineSegment StartX=51.2878 StartY=18.1587 StartZ=0 EndX=51.2878 EndY=18.2275 EndZ=0
    g292: LineSegment StartX=51.2878 StartY=18.2275 StartZ=0 EndX=51.2232 EndY=18.2275 EndZ=0
    g293: LineSegment StartX=51.2232 StartY=18.2275 StartZ=0 EndX=51.2267 EndY=18.2921 EndZ=0
    g294: LineSegment StartX=51.2267 StartY=18.2921 StartZ=0 EndX=51.1526 EndY=18.2921 EndZ=0
    g295: LineSegment StartX=51.1526 StartY=18.2921 StartZ=0 EndX=51.1526 EndY=18.3662 EndZ=0
    g296: LineSegment StartX=51.1526 StartY=18.3662 StartZ=0 EndX=51.0845 EndY=18.3602 EndZ=0
    g297: LineSegment StartX=51.0845 StartY=18.3602 StartZ=0 EndX=51.0845 EndY=18.4424 EndZ=0
    g298: LineSegment StartX=51.0845 StartY=18.4424 StartZ=0 EndX=51.0222 EndY=18.4424 EndZ=0
    g299: LineSegment StartX=51.0222 StartY=18.4424 StartZ=0 EndX=51.0222 EndY=18.5138 EndZ=0
    g300: LineSegment StartX=51.0222 StartY=18.5138 StartZ=0 EndX=50.8169 EndY=18.5138 EndZ=0
    g301: LineSegment StartX=50.8169 StartY=18.5138 StartZ=0 EndX=50.7878 EndY=18.6026 EndZ=0
    g302: LineSegment StartX=50.7878 StartY=18.6026 StartZ=0 EndX=50.7494 EndY=18.6113 EndZ=0
    g303: LineSegment StartX=50.7494 StartY=18.6113 StartZ=0 EndX=50.7397 EndY=18.6731 EndZ=0
    g304: LineSegment StartX=50.7397 StartY=18.6731 StartZ=0 EndX=50.5414 EndY=18.6536 EndZ=0
    g305: LineSegment StartX=50.5414 StartY=18.6536 StartZ=0 EndX=50.5381 EndY=18.7381 EndZ=0
    g306: LineSegment StartX=50.5381 StartY=18.7381 StartZ=0 EndX=50.4114 EndY=18.7218 EndZ=0
    g307: LineSegment StartX=50.4114 StartY=18.7218 StartZ=0 EndX=50.3951 EndY=18.7934 EndZ=0
    g308: LineSegment StartX=50.3951 StartY=18.7934 StartZ=0 EndX=50.3334 EndY=18.7934 EndZ=0
    g309: LineSegment StartX=50.3334 StartY=18.7934 StartZ=0 EndX=50.3366 EndY=18.8389 EndZ=0
    g310: LineSegment StartX=50.3366 StartY=18.8389 StartZ=0 EndX=50.2066 EndY=18.8389 EndZ=0
    g311: LineSegment StartX=50.2066 StartY=18.8389 StartZ=0 EndX=50.2099 EndY=18.9201 EndZ=0
    g312: LineSegment StartX=50.2099 StartY=18.9201 StartZ=0 EndX=50.1254 EndY=18.9266 EndZ=0
    g313: LineSegment StartX=50.1254 StartY=18.9266 StartZ=0 EndX=50.1156 EndY=19.0046 EndZ=0
    g314: LineSegment StartX=50.1156 StartY=19.0046 StartZ=0 EndX=49.9986 EndY=18.9949 EndZ=0
    g315: LineSegment StartX=49.9986 StartY=18.9949 StartZ=0 EndX=49.9921 EndY=19.0859 EndZ=0
    g316: LineSegment StartX=49.9921 StartY=19.0859 StartZ=0 EndX=49.9368 EndY=19.0501 EndZ=0
    g317: LineSegment StartX=49.9368 StartY=19.0501 StartZ=0 EndX=49.9206 EndY=19.1509 EndZ=0
    g318: LineSegment StartX=49.9206 StartY=19.1509 StartZ=0 EndX=49.7971 EndY=19.1281 EndZ=0
    g319: LineSegment StartX=49.7971 StartY=19.1281 StartZ=0 EndX=49.8068 EndY=19.2029 EndZ=0
    g320: LineSegment StartX=49.8068 StartY=19.2029 StartZ=0 EndX=49.7288 EndY=19.1899 EndZ=0
    g321: LineSegment StartX=49.7288 StartY=19.1899 StartZ=0 EndX=49.7191 EndY=19.2582 EndZ=0
    g322: LineSegment StartX=49.7191 StartY=19.2582 StartZ=0 EndX=49.6606 EndY=19.2647 EndZ=0
    g323: LineSegment StartX=49.6606 StartY=19.2647 StartZ=0 EndX=49.6541 EndY=19.3329 EndZ=0
    g324: LineSegment StartX=49.6541 StartY=19.3329 StartZ=0 EndX=49.6021 EndY=19.3329 EndZ=0
    g325: LineSegment StartX=49.6021 StartY=19.3329 StartZ=0 EndX=49.5988 EndY=19.4077 EndZ=0
    g326: LineSegment StartX=49.5988 StartY=19.4077 StartZ=0 EndX=49.4623 EndY=19.3947 EndZ=0
    g327: LineSegment StartX=49.4623 StartY=19.3947 StartZ=0 EndX=49.4623 EndY=19.4727 EndZ=0
    g328: LineSegment StartX=49.4623 StartY=19.4727 StartZ=0 EndX=49.2543 EndY=19.4532 EndZ=0
    g329: LineSegment StartX=49.2543 StartY=19.4532 StartZ=0 EndX=49.2543 EndY=19.5279 EndZ=0
    g330: LineSegment StartX=49.2543 StartY=19.5279 StartZ=0 EndX=49.199 EndY=19.5279 EndZ=0
    g331: LineSegment StartX=49.199 StartY=19.5279 StartZ=0 EndX=49.199 EndY=19.6189 EndZ=0
    g332: LineSegment StartX=49.199 StartY=19.6189 StartZ=0 EndX=49.0658 EndY=19.6059 EndZ=0
    g333: LineSegment StartX=49.0658 StartY=19.6059 StartZ=0 EndX=49.0495 EndY=19.6612 EndZ=0
    g334: LineSegment StartX=49.0495 StartY=19.6612 StartZ=0 EndX=48.991 EndY=19.6547 EndZ=0
    g335: LineSegment StartX=48.991 StartY=19.6547 StartZ=0 EndX=48.9845 EndY=19.7359 EndZ=0
    g336: LineSegment StartX=48.9845 StartY=19.7359 StartZ=0 EndX=48.8577 EndY=19.7262 EndZ=0
    g337: LineSegment StartX=48.8577 StartY=19.7262 StartZ=0 EndX=48.8577 EndY=19.8149 EndZ=0
    g338: LineSegment StartX=48.8577 StartY=19.8149 StartZ=0 EndX=48.7743 EndY=19.8069 EndZ=0
    g339: LineSegment StartX=48.7743 StartY=19.8069 StartZ=0 EndX=48.7743 EndY=19.8894 EndZ=0
    g340: LineSegment StartX=48.7743 StartY=19.8894 StartZ=0 EndX=48.5854 EndY=19.8894 EndZ=0
    g341: LineSegment StartX=48.5854 StartY=19.8894 StartZ=0 EndX=48.5854 EndY=19.9533 EndZ=0
    g342: LineSegment StartX=48.5854 StartY=19.9533 StartZ=0 EndX=48.4417 EndY=19.9533 EndZ=0
    g343: LineSegment StartX=48.4417 StartY=19.9533 StartZ=0 EndX=48.4417 EndY=20.0118 EndZ=0
    g344: LineSegment StartX=48.4417 StartY=20.0118 StartZ=0 EndX=48.3751 EndY=20.0118 EndZ=0
    g345: LineSegment StartX=48.3751 StartY=20.0118 StartZ=0 EndX=48.3751 EndY=20.089 EndZ=0
    g346: LineSegment StartX=48.3751 StartY=20.089 StartZ=0 EndX=48.3033 EndY=20.089 EndZ=0
    g347: LineSegment StartX=48.3033 StartY=20.089 StartZ=0 EndX=48.3033 EndY=20.1524 EndZ=0
    g348: LineSegment StartX=48.3033 StartY=20.1524 StartZ=0 EndX=48.0916 EndY=20.1524 EndZ=0
    g349: LineSegment StartX=48.0916 StartY=20.1524 StartZ=0 EndX=48.0916 EndY=20.2331 EndZ=0
    g350: LineSegment StartX=48.0916 StartY=20.2331 StartZ=0 EndX=47.8912 EndY=20.2331 EndZ=0
    g351: LineSegment StartX=47.8912 StartY=20.2331 StartZ=0 EndX=47.8912 EndY=20.2962 EndZ=0
    g352: LineSegment StartX=47.8912 StartY=20.2962 StartZ=0 EndX=47.6864 EndY=20.2962 EndZ=0
    g353: LineSegment StartX=47.6864 StartY=20.2962 StartZ=0 EndX=47.6864 EndY=20.3681 EndZ=0
    g354: LineSegment StartX=47.6864 StartY=20.3681 StartZ=0 EndX=47.2898 EndY=20.3681 EndZ=0
    g355: LineSegment StartX=47.2898 StartY=20.3681 StartZ=0 EndX=47.2898 EndY=20.4313 EndZ=0
    g356: LineSegment StartX=47.2898 StartY=20.4313 StartZ=0 EndX=47.0094 EndY=20.4313 EndZ=0
    g357: LineSegment StartX=47.0094 StartY=20.4313 StartZ=0 EndX=47.0094 EndY=20.5033 EndZ=0
    g358: LineSegment StartX=47.0094 StartY=20.5033 StartZ=0 EndX=46.7265 EndY=20.5033 EndZ=0
    g359: LineSegment StartX=46.7265 StartY=20.5033 StartZ=0 EndX=46.7265 EndY=20.5623 EndZ=0
    g360: LineSegment StartX=46.7265 StartY=20.5623 StartZ=0 EndX=46.3195 EndY=20.5623 EndZ=0
    g361: LineSegment StartX=46.3195 StartY=20.5623 StartZ=0 EndX=46.2304 EndY=20.478 EndZ=0
    g362: LineSegment StartX=46.2304 StartY=20.478 StartZ=0 EndX=45.8403 EndY=20.478 EndZ=0
    g363: LineSegment StartX=45.8403 StartY=20.478 StartZ=0 EndX=45.7581 EndY=20.3987 EndZ=0
    g364: LineSegment StartX=45.7581 StartY=20.3987 StartZ=0 EndX=45.6847 EndY=20.3987 EndZ=0
    g365: LineSegment StartX=45.6847 StartY=20.3987 StartZ=0 EndX=45.6847 EndY=20.4757 EndZ=0
    g366: LineSegment StartX=45.6847 StartY=20.4757 StartZ=0 EndX=45.2353 EndY=20.4757 EndZ=0
    g367: LineSegment StartX=45.2353 StartY=20.4757 StartZ=0 EndX=45.1511 EndY=20.3964 EndZ=0
    g368: LineSegment StartX=45.1511 StartY=20.3964 StartZ=0 EndX=45.039 EndY=20.3905 EndZ=0
    g369: LineSegment StartX=45.1271 StartY=20.498 StartZ=0 EndX=45.039 EndY=20.3905 EndZ=0
    g370: LineSegment StartX=45.1271 StartY=20.498 StartZ=0 EndX=45.1672 EndY=20.498 EndZ=0
    g371: LineSegment StartX=45.1672 StartY=20.498 StartZ=0 EndX=45.2586 EndY=20.5605 EndZ=0
    g372: LineSegment StartX=45.2586 StartY=20.5605 StartZ=0 EndX=45.3242 EndY=20.5605 EndZ=0
    g373: LineSegment StartX=45.3242 StartY=20.5605 StartZ=0 EndX=45.4009 EndY=20.6461 EndZ=0
    g374: LineSegment StartX=45.4009 StartY=20.6461 StartZ=0 EndX=45.5221 EndY=20.6461 EndZ=0
    g375: LineSegment StartX=45.5221 StartY=20.6461 StartZ=0 EndX=45.6149 EndY=20.705 EndZ=0
    g376: LineSegment StartX=45.6149 StartY=20.705 StartZ=0 EndX=45.8042 EndY=20.705 EndZ=0
    g377: LineSegment StartX=45.8042 StartY=20.705 StartZ=0 EndX=45.9915 EndY=20.8898 EndZ=0
    g378: LineSegment StartX=45.9915 StartY=20.8898 StartZ=0 EndX=45.9915 EndY=20.959 EndZ=0
    g379: LineSegment StartX=45.9915 StartY=20.959 StartZ=0 EndX=46.0581 EndY=21.0202 EndZ=0
    g380: LineSegment StartX=46.0581 StartY=21.0202 StartZ=0 EndX=46.0527 EndY=21.0894 EndZ=0
    g381: LineSegment StartX=46.0527 StartY=21.0894 StartZ=0 EndX=46.2124 EndY=21.2464 EndZ=0
    g382: LineSegment StartX=46.2124 StartY=21.2464 StartZ=0 EndX=46.2763 EndY=21.2277 EndZ=0
    g383: LineSegment StartX=46.2763 StartY=21.2277 StartZ=0 EndX=46.5051 EndY=21.4486 EndZ=0
    g384: LineSegment StartX=46.5051 StartY=21.4486 StartZ=0 EndX=46.585 EndY=21.4539 EndZ=0
    g385: LineSegment StartX=46.585 StartY=21.4539 StartZ=0 EndX=46.6994 EndY=21.603 EndZ=0
    g386: LineSegment StartX=46.6994 StartY=21.603 StartZ=0 EndX=46.8245 EndY=21.5843 EndZ=0
    g387: LineSegment StartX=46.8245 StartY=21.5843 StartZ=0 EndX=46.9016 EndY=21.6855 EndZ=0
    g388: LineSegment StartX=46.9016 StartY=21.6855 StartZ=0 EndX=46.9655 EndY=21.6562 EndZ=0
    g389: LineSegment StartX=46.9655 StartY=21.6562 StartZ=0 EndX=47.205 EndY=21.8754 EndZ=0
    g390: LineSegment StartX=47.205 StartY=21.8754 StartZ=0 EndX=47.205 EndY=22.0711 EndZ=0
    g391: LineSegment StartX=47.205 StartY=22.0711 StartZ=0 EndX=47.2634 EndY=22.0711 EndZ=0
    g392: LineSegment StartX=47.2634 StartY=22.0711 StartZ=0 EndX=47.6208 EndY=22.4458 EndZ=0
    g393: LineSegment StartX=47.6208 StartY=22.4458 StartZ=0 EndX=47.6208 EndY=22.5177 EndZ=0
    g394: LineSegment StartX=47.6208 StartY=22.5177 StartZ=0 EndX=47.8212 EndY=22.7182 EndZ=0
    g395: LineSegment StartX=47.8212 StartY=22.7182 StartZ=0 EndX=47.8343 EndY=22.7944 EndZ=0
    g396: LineSegment StartX=47.8343 StartY=22.7944 StartZ=0 EndX=48.0478 EndY=22.997 EndZ=0
    g397: LineSegment StartX=48.0478 StartY=22.997 StartZ=0 EndX=48.0478 EndY=23.1365 EndZ=0
    g398: LineSegment StartX=48.0478 StartY=23.1365 StartZ=0 EndX=48.0998 EndY=23.2173 EndZ=0
    g399: LineSegment StartX=48.0998 StartY=23.2173 StartZ=0 EndX=48.0998 EndY=23.2802 EndZ=0
    ... +484 more geometry lines
  constraints (1492):
    c: Coincident(g3,g2)
    c: Vertical(g4)
    c: Vertical(g6)
    c: Coincident(g8,g7)
    c: Vertical(g8)
    c: Coincident(g8,g9)
    c: Coincident(g9,g10)
    c: Vertical(g10)
    c: Coincident(g10,g11)
    c: Coincident(g11,g12)
    c: Vertical(g12)
    c: Coincident(g13,g12)
    c: Horizontal(g13)
    c: Vertical(g14)
    c: Coincident(g16,g15)
    c: Vertical(g16)
    c: Horizontal(g17)
    c: Coincident(g18,g17)
    c: Vertical(g18)
    c: Horizontal(g19)
    c: Coincident(g20,g19)
    c: Vertical(g20)
    c: Horizontal(g21)
    c: Vertical(g22)
    c: Horizontal(g23)
    c: Coincident(g24,g23)
    c: Vertical(g24)
    c: Horizontal(g25)
    c: Coincident(g27,g26)
    c: Horizontal(g27)
    c: Vertical(g28)
    c: Coincident(g30,g29)
    c: Vertical(g30)
    c: Coincident(g31,g32)
    c: Vertical(g32)
    c: Coincident(g32,g33)
    c: Horizontal(g33)
    c: Coincident(g34,g33)
    c: Vertical(g34)
    c: Coincident(g35,g34)
    c: Horizontal(g35)
    c: Coincident(g36,g35)
    c: Vertical(g36)
    c: Coincident(g37,g36)
    c: Horizontal(g37)
    c: Vertical(g38)
    c: Horizontal(g39)
    c: Vertical(g40)
    c: Horizontal(g41)
    c: Coincident(g42,g41)
    c: Vertical(g42)
    c: Horizontal(g43)
    c: Coincident(g44,g43)
    c: Vertical(g44)
    c: Coincident(g45,g44)
    c: Horizontal(g45)
    c: Coincident(g46,g45)
    c: Vertical(g46)
    c: Coincident(g47,g46)
    c: Horizontal(g47)
    c: Coincident(g48,g47)
    c: Vertical(g48)
    c: Horizontal(g49)
    c: Vertical(g50)
    c: Coincident(g51,g50)
    c: Horizontal(g51)
    c: Vertical(g52)
    c: Coincident(g53,g52)
    c: Horizontal(g53)
    c: Coincident(g54,g53)
    c: Vertical(g54)
    c: Coincident(g55,g54)
    c: Horizontal(g55)
    c: Coincident(g56,g55)
    c: Vertical(g56)
    c: Coincident(g57,g56)
    c: Horizontal(g57)
    c: Coincident(g58,g57)
    c: Vertical(g58)
    c: Coincident(g60,g59)
    c: Vertical(g60)
    c: Coincident(g61,g60)
    c: Horizontal(g61)
    c: Vertical(g62)
    c: Horizontal(g63)
    c: Coincident(g64,g63)
    c: Vertical(g64)
    c: Horizontal(g65)
    c: Vertical(g66)
    c: Coincident(g68,g67)
    c: Vertical(g68)
    c: Horizontal(g69)
    c: Coincident(g70,g69)
    c: Vertical(g70)
    c: Horizontal(g71)
    c: Coincident(g72,g71)
    c: Vertical(g72)
    c: Horizontal(g73)
    c: Coincident(g74,g73)
    c: Vertical(g74)
    c: Horizontal(g75)
    c: Coincident(g76,g75)
    c: Vertical(g76)
    c: Horizontal(g77)
    c: Vertical(g78)
    c: Coincident(g79,g78)
    c: Coincident(g80,g79)
    c: Vertical(g80)
    c: Coincident(g81,g80)
    c: Coincident(g82,g81)
    c: Horizontal(g83)
    c: Coincident(g85,g84)
    c: Horizontal(g85)
    c: Coincident(g86,g85)
    c: Coincident(g89,g88)
    c: Horizontal(g89)
    c: Coincident(g90,g89)
    c: Coincident(g91,g90)
    c: Horizontal(g91)
    c: Coincident(g92,g91)
    c: Horizontal(g93)
    c: Coincident(g94,g93)
    c: Horizontal(g95)
    c: Coincident(g96,g95)
    c: Coincident(g97,g98)
    c: Coincident(g98,g99)
    c: Vertical(g99)
    c: Coincident(g99,g100)
    c: Coincident(g100,g101)
    c: Coincident(g101,g102)
    c: Coincident(g102,g103)
    c: Coincident(g103,g104)
    c: Coincident(g104,g105)
    c: Vertical(g105)
    c: Coincident(g105,g106)
    c: Coincident(g106,g107)
    c: Coincident(g107,g108)
    c: Horizontal(g108)
    c: Coincident(g108,g109)
    c: Coincident(g109,g110)
    c: Vertical(g110)
    c: Coincident(g110,g111)
    c: Coincident(g111,g112)
    c: Coincident(g112,g113)
    c: Coincident(g113,g114)
    c: Coincident(g114,g115)
    c: Coincident(g115,g116)
    c: Vertical(g116)
    c: Coincident(g116,g117)
    c: Coincident(g117,g118)
    c: Coincident(g118,g119)
    c: Coincident(g119,g120)
    c: Coincident(g120,g121)
    c: Horizontal(g121)
    c: Coincident(g121,g122)
    c: Coincident(g122,g123)
    c: Coincident(g123,g124)
    c: Coincident(g124,g125)
    c: Vertical(g125)
    c: Coincident(g125,g126)
    c: Coincident(g126,g127)
    c: Horizontal(g127)
    c: Coincident(g127,g128)
    c: Vertical(g128)
    c: Coincident(g128,g129)
    c: Coincident(g129,g130)
    c: Vertical(g130)
    c: Coincident(g130,g131)
    c: Horizontal(g131)
    c: Coincident(g131,g132)
    c: Vertical(g132)
    c: Coincident(g132,g133)
    c: Coincident(g133,g134)
    c: Coincident(g134,g135)
    c: Coincident(g135,g136)
    c: Coincident(g136,g137)
    c: Coincident(g137,g138)
    c: Vertical(g138)
    c: Coincident(g138,g139)
    c: Coincident(g139,g140)
    c: Vertical(g140)
    c: Coincident(g140,g141)
    c: Horizontal(g141)
    c: Coincident(g141,g142)
    c: Coincident(g142,g143)
    c: Coincident(g143,g144)
    c: Coincident(g144,g145)
    c: Coincident(g145,g146)
    c: Vertical(g146)
    c: Coincident(g146,g147)
    c: Coincident(g147,g148)
    c: Vertical(g148)
    c: Coincident(g148,g149)
    c: Horizontal(g149)
    c: Coincident(g149,g150)
    c: Vertical(g150)
    c: Coincident(g150,g151)
    c: Horizontal(g151)
    c: Coincident(g151,g152)
    c: Vertical(g152)
    c: Coincident(g152,g153)
    c: Horizontal(g153)
    c: Coincident(g153,g154)
    c: Vertical(g154)
    c: Coincident(g154,g155)
    c: Horizontal(g155)
    c: Coincident(g155,g156)
    c: Vertical(g156)
    c: Coincident(g156,g157)
    c: Horizontal(g157)
    c: Coincident(g157,g158)
    c: Vertical(g158)
    c: Coincident(g158,g159)
    c: Coincident(g159,g160)
    c: Coincident(g160,g161)
    c: Horizontal(g161)
    c: Coincident(g161,g162)
    c: Vertical(g162)
    c: Coincident(g162,g163)
    c: Horizontal(g163)
    c: Coincident(g163,g164)
    c: Coincident(g164,g165)
    c: Horizontal(g165)
    c: Coincident(g165,g166)
    c: Vertical(g166)
    c: Coincident(g166,g167)
    c: Horizontal(g167)
    c: Coincident(g167,g168)
    c: Coincident(g168,g169)
    c: Coincident(g169,g170)
    c: Vertical(g170)
    c: Coincident(g170,g171)
    c: Coincident(g171,g172)
    c: Vertical(g172)
    c: Coincident(g172,g173)
    c: Horizontal(g173)
    c: Coincident(g173,g174)
    c: Vertical(g174)
    c: Coincident(g174,g175)
    c: Horizontal(g175)
    c: Coincident(g175,g176)
    c: Vertical(g176)
    c: Coincident(g176,g177)
    c: Coincident(g177,g178)
    c: Vertical(g178)
    c: Coincident(g178,g179)
    c: Horizontal(g179)
    c: Coincident(g179,g180)
    c: Vertical(g180)
    c: Coincident(g180,g181)
    c: Horizontal(g181)
    c: Coincident(g181,g182)
    c: Vertical(g182)
    c: Coincident(g182,g183)
    c: Horizontal(g183)
    c: Coincident(g183,g184)
    c: Vertical(g184)
    c: Coincident(g184,g185)
    c: Horizontal(g185)
    c: Coincident(g185,g186)
    c: Coincident(g186,g187)
    c: Coincident(g187,g188)
    c: Coincident(g188,g189)
    c: Vertical(g189)
    c: Coincident(g189,g190)
    c: Coincident(g190,g191)
    c: Coincident(g191,g192)
    c: Coincident(g192,g193)
    c: Coincident(g193,g194)
    c: Coincident(g194,g195)
    c: Vertical(g195)
    c: Coincident(g195,g196)
    c: Coincident(g196,g197)
    c: Vertical(g197)
    c: Coincident(g197,g198)
    c: Coincident(g198,g199)
    c: Vertical(g199)
    c: Coincident(g199,g200)
    c: Coincident(g200,g201)
    c: Vertical(g201)
    c: Coincident(g201,g202)
    c: Coincident(g202,g203)
    c: Vertical(g203)
    c: Coincident(g203,g204)
    c: Coincident(g204,g205)
    c: Vertical(g205)
    c: Coincident(g205,g206)
    c: Coincident(g206,g207)
    c: Coincident(g207,g208)
    c: Coincident(g208,g209)
    c: Vertical(g209)
    c: Coincident(g209,g210)
    c: Coincident(g210,g211)
    c: Coincident(g211,g212)
    c: Coincident(g212,g213)
    c: Coincident(g213,g214)
    c: Coincident(g214,g215)
    c: Vertical(g215)
    c: Coincident(g215,g216)
    c: Coincident(g216,g217)
    c: Horizontal(g217)
    c: Coincident(g217,g218)
    c: Vertical(g218)
    c: Coincident(g218,g219)
    c: Horizontal(g219)
    c: Coincident(g219,g220)
    c: Coincident(g220,g221)
    c: Horizontal(g221)
    c: Coincident(g221,g222)
    c: Coincident(g222,g223)
    c: Horizontal(g223)
    c: Coincident(g223,g224)
    c: Coincident(g224,g225)
    c: Horizontal(g225)
    c: Coincident(g225,g226)
    c: Vertical(g226)
    c: Coincident(g226,g227)
    c: Horizontal(g227)
    c: Coincident(g227,g228)
    c: Vertical(g228)
    c: Coincident(g228,g229)
    c: Horizontal(g229)
    c: Coincident(g229,g230)
    c: Coincident(g230,g231)
    c: Coincident(g231,g232)
    c: Coincident(g232,g233)
    c: Horizontal(g233)
    c: Coincident(g233,g234)
    c: Coincident(g234,g235)
    c: Horizontal(g235)
    c: Coincident(g235,g236)
    c: Coincident(g236,g237)
    c: Horizontal(g237)
    c: Coincident(g237,g238)
    c: Coincident(g238,g239)
    c: Horizontal(g239)
    c: Coincident(g239,g240)
    c: Coincident(g240,g241)
    c: Vertical(g241)
    c: Coincident(g241,g242)
    c: Horizontal(g242)
    c: Coincident(g242,g243)
    c: Vertical(g243)
    c: Coincident(g243,g244)
    c: Coincident(g244,g245)
    c: Vertical(g245)
    c: Coincident(g245,g246)
    c: Horizontal(g246)
    c: Coincident(g246,g247)
    c: Coincident(g247,g248)
    c: Horizontal(g248)
    c: Coincident(g248,g249)
    c: Vertical(g249)
    c: Coincident(g249,g250)
    c: Coincident(g250,g251)
    c: Coincident(g251,g252)
    c: Horizontal(g252)
    c: Coincident(g252,g253)
    c: Coincident(g253,g254)
    c: Horizontal(g254)
    c: Coincident(g254,g255)
    c: Vertical(g255)
    c: Coincident(g255,g256)
    c: Coincident(g256,g257)
    c: Coincident(g257,g258)
    c: Coincident(g258,g259)
    c: Coincident(g259,g260)
    c: Coincident(g260,g261)
    c: Vertical(g257)
    c: Horizontal(g258)
    c: Horizontal(g256)
    c: Vertical(g259)
    c: Horizontal(g260)
    c: Vertical(g261)
    c: Coincident(g261,g262)
    c: Horizontal(g262)
    c: Coincident(g262,g263)
    c: Vertical(g263)
    c: Coincident(g263,g264)
    c: Coincident(g264,g265)
    c: Coincident(g265,g266)
    c: Coincident(g266,g267)
    c: Coincident(g267,g268)
    c: Coincident(g268,g269)
    c: Vertical(g269)
    c: Coincident(g269,g270)
    c: Horizontal(g270)
    c: Coincident(g270,g271)
    c: Vertical(g271)
    c: Coincident(g271,g272)
    c: Coincident(g272,g273)
    c: Vertical(g273)
    c: Coincident(g273,g274)
    c: Horizontal(g274)
    c: Coincident(g274,g275)
    c: Vertical(g275)
    c: Coincident(g275,g276)
    c: Horizontal(g276)
    c: Coincident(g276,g277)
    c: Coincident(g277,g278)
    c: Horizontal(g278)
    c: Coincident(g278,g279)
    c: Coincident(g279,g280)
    c: Coincident(g280,g281)
    c: Vertical(g281)
    c: Coincident(g281,g282)
    c: Coincident(g282,g283)
    c: Coincident(g283,g284)
    c: Horizontal(g284)
    c: Coincident(g284,g285)
    c: Coincident(g285,g286)
    c: Coincident(g286,g287)
    c: Coincident(g287,g288)
    c: Coincident(g288,g289)
    c: Coincident(g289,g290)
    c: Coincident(g290,g291)
    c: Vertical(g291)
    c: Coincident(g291,g292)
    c: Horizontal(g292)
    c: Coincident(g292,g293)
    c: Coincident(g293,g294)
    c: Horizontal(g294)
    c: Coincident(g294,g295)
    c: Vertical(g295)
    c: Coincident(g295,g296)
    c: Coincident(g296,g297)
    c: Vertical(g297)
    c: Coincident(g297,g298)
    c: Horizontal(g298)
    c: Coincident(g298,g299)
    c: Vertical(g299)
    c: Coincident(g299,g300)
    c: Horizontal(g300)
    c: Coincident(g300,g301)
    c: Coincident(g301,g302)
    c: Coincident(g302,g303)
    c: Coincident(g303,g304)
    c: Coincident(g304,g305)
    c: Coincident(g305,g306)
    c: Coincident(g306,g307)
    c: Coincident(g307,g308)
    c: Horizontal(g308)
    c: Coincident(g308,g309)
    c: Coincident(g309,g310)
    c: Horizontal(g310)
    c: Coincident(g310,g311)
    c: Coincident(g311,g312)
    c: Coincident(g312,g313)
    c: Coincident(g313,g314)
    c: Coincident(g314,g315)
    c: Coincident(g315,g316)
    c: Coincident(g316,g317)
    c: Coincident(g317,g318)
    c: Coincident(g318,g319)
    c: Coincident(g319,g320)
    c: Coincident(g320,g321)
    c: Coincident(g321,g322)
    c: Coincident(g322,g323)
    c: Coincident(g323,g324)
    c: Horizontal(g324)
    c: Coincident(g324,g325)
    c: Coincident(g325,g326)
    c: Coincident(g326,g327)
    c: Vertical(g327)
    c: Coincident(g327,g328)
    c: Coincident(g328,g329)
    c: Coincident(g329,g330)
    c: Coincident(g330,g331)
    c: Vertical(g331)
    c: Coincident(g331,g332)
    c: Coincident(g332,g333)
    c: Coincident(g333,g334)
    c: Coincident(g334,g335)
    c: Coincident(g335,g336)
    c: Coincident(g336,g337)
    c: Vertical(g337)
    c: Coincident(g337,g338)
    c: Coincident(g338,g339)
    c: Coincident(g339,g340)
    c: Coincident(g340,g341)
    c: Coincident(g341,g342)
    c: Coincident(g342,g343)
    c: Coincident(g343,g344)
    c: Coincident(g344,g345)
    c: Coincident(g345,g346)
    c: Coincident(g346,g347)
    c: Coincident(g347,g348)
    c: Coincident(g348,g349)
    c: Coincident(g349,g350)
    c: Coincident(g350,g351)
    c: Coincident(g351,g352)
    c: Coincident(g352,g353)
    c: Coincident(g353,g354)
    c: Coincident(g354,g355)
    c: Coincident(g355,g356)
    c: Coincident(g356,g357)
    c: Vertical(g357)
    c: Coincident(g357,g358)
    c: Horizontal(g358)
    c: Coincident(g358,g359)
    c: Coincident(g359,g360)
    c: Coincident(g360,g361)
    c: Coincident(g361,g362)
    c: Horizontal(g362)
    c: Coincident(g362,g363)
    c: Coincident(g363,g364)
    c: Coincident(g364,g365)
    c: Coincident(g365,g366)
    c: Coincident(g366,g367)
    c: Horizontal(g290)
    c: Vertical(g287)
    c: Vertical(g285)
    c: Vertical(g283)
    c: Vertical(g279)
    c: Vertical(g277)
    c: Horizontal(g286)
    c: Horizontal(g288)
    c: Vertical(g289)
    c: Horizontal(g280)
    c: Horizontal(g282)
    c: Vertical(g329)
    c: Horizontal(g330)
    c: Horizontal(g340)
    c: Horizontal(g342)
    c: Horizontal(g344)
    c: Horizontal(g346)
    c: Horizontal(g348)
    c: Horizontal(g350)
    c: Vertical(g339)
    c: Vertical(g341)
    c: Vertical(g343)
    c: Vertical(g345)
    c: Vertical(g347)
    c: Vertical(g349)
    c: Vertical(g351)
    c: Vertical(g353)
    c: Vertical(g355)
    c: Horizontal(g352)
    c: Horizontal(g354)
    c: Horizontal(g356)
    c: Vertical(g359)
    c: Horizontal(g360)
    c: Horizontal(g364)
    c: Vertical(g365)
    c: Horizontal(g366)
    c: Coincident(g368,g367)
    c: Coincident(g369,g368)
    c: Coincident(g369,g370)
    c: Coincident(g370,g371)
    c: Coincident(g371,g372)
    c: Horizontal(g372)
    c: Coincident(g372,g373)
    c: Coincident(g373,g374)
    c: Coincident(g374,g375)
    c: Coincident(g375,g376)
    c: Coincident(g376,g377)
    c: Coincident(g377,g378)
    c: Vertical(g378)
    c: Coincident(g378,g379)
    c: Coincident(g379,g380)
    c: Coincident(g380,g381)
    c: Coincident(g381,g382)
    c: Coincident(g382,g383)
    c: Coincident(g383,g384)
    c: Coincident(g384,g385)
    c: Coincident(g385,g386)
    c: Coincident(g386,g387)
    c: Coincident(g387,g388)
    c: Coincident(g388,g389)
    c: Coincident(g389,g390)
    c: Coincident(g390,g391)
    c: Horizontal(g391)
    c: Coincident(g391,g392)
    c: Coincident(g392,g393)
    c: Coincident(g393,g394)
    c: Coincident(g394,g395)
    c: Coincident(g395,g396)
    c: Coincident(g396,g397)
    c: Coincident(g397,g398)
    c: Coincident(g398,g399)
    c: Coincident(g399,g400)
    c: Coincident(g400,g401)
    c: Coincident(g401,g402)
    c: Coincident(g402,g403)
    c: Coincident(g403,g404)
    c: Coincident(g404,g405)
    c: Coincident(g405,g406)
    c: Coincident(g406,g407)
    c: Coincident(g407,g408)
    c: Coincident(g408,g409)
    c: Vertical(g409)
    c: Coincident(g409,g410)
    c: Coincident(g410,g411)
    c: Vertical(g411)
    c: Coincident(g411,g412)
    c: Horizontal(g412)
    c: Coincident(g412,g413)
    c: Coincident(g413,g414)
    c: Horizontal(g414)
    c: Coincident(g414,g415)
    c: Coincident(g415,g416)
    c: Coincident(g416,g417)
    c: Coincident(g417,g418)
    c: Coincident(g418,g419)
    c: Coincident(g419,g420)
    c: Coincident(g420,g421)
    c: Coincident(g421,g422)
    c: Coincident(g422,g423)
    c: Coincident(g423,g424)
    c: Coincident(g424,g425)
    c: Coincident(g425,g426)
    c: Horizontal(g426)
    c: Coincident(g426,g427)
    c: Coincident(g427,g428)
    c: Horizontal(g428)
    c: Coincident(g428,g429)
    c: Coincident(g429,g430)
    c: Coincident(g430,g431)
    c: Coincident(g431,g432)
    c: Horizontal(g432)
    c: Coincident(g432,g433)
    c: Coincident(g433,g434)
    c: Horizontal(g434)
    c: Coincident(g434,g435)
    c: Coincident(g435,g436)
    c: Coincident(g436,g437)
    c: Coincident(g437,g438)
    c: Coincident(g439,g440)
    c: Coincident(g440,g441)
    c: Coincident(g441,g442)
    c: Coincident(g442,g443)
    c: Coincident(g443,g444)
    c: Coincident(g444,g445)
    c: Coincident(g445,g446)
    c: Coincident(g446,g447)
    c: Coincident(g447,g448)
    c: Coincident(g448,g449)
    c: Coincident(g449,g450)
    c: Coincident(g450,g451)
    c: Coincident(g451,g452)
    c: Coincident(g452,g453)
    c: Coincident(g453,g454)
    c: Coincident(g454,g455)
    c: Coincident(g455,g456)
    c: Coincident(g456,g457)
    c: Coincident(g457,g458)
    c: Coincident(g458,g459)
    c: Coincident(g459,g460)
    c: Coincident(g460,g461)
    c: Coincident(g461,g462)
    c: Coincident(g462,g463)
    c: Coincident(g463,g464)
    c: Coincident(g464,g465)
    c: Coincident(g465,g466)
    c: Coincident(g466,g467)
    c: Coincident(g467,g468)
    c: Coincident(g468,g469)
    c: Coincident(g469,g470)
    c: Coincident(g470,g471)
    c: Coincident(g471,g472)
    c: Horizontal(g472)
    c: Coincident(g472,g473)
    c: Coincident(g473,g474)
    c: Coincident(g474,g475)
    c: Coincident(g475,g476)
    c: Coincident(g476,g477)
    c: Coincident(g477,g478)
    c: Coincident(g478,g479)
    c: Coincident(g479,g480)
    c: Coincident(g480,g481)
    c: Coincident(g481,g482)
    c: Coincident(g482,g483)
    c: Coincident(g483,g484)
    c: Coincident(g484,g485)
    c: Coincident(g485,g486)
    c: Coincident(g486,g487)
    c: Coincident(g487,g488)
    c: Vertical(g488)
    c: Coincident(g488,g489)
    c: Coincident(g489,g490)
    c: Vertical(g490)
    c: Coincident(g490,g491)
    c: Coincident(g491,g492)
    c: Coincident(g492,g493)
    c: Coincident(g493,g494)
    c: Coincident(g494,g495)
    c: Coincident(g495,g496)
    c: Coincident(g496,g497)
    c: Coincident(g497,g498)
    c: Coincident(g498,g499)
    c: Coincident(g499,g500)
    c: Coincident(g500,g501)
    c: Coincident(g501,g502)
    c: Coincident(g502,g503)
    c: Coincident(g503,g504)
    c: Horizontal(g370)
    c: Horizontal(g374)
    c: Horizontal(g376)
    c: Vertical(g390)
    c: Vertical(g397)
    c: Vertical(g399)
    c: Vertical(g401)
    c: Vertical(g403)
    c: Vertical(g407)
    c: Horizontal(g410)
    c: Vertical(g413)
    c: Vertical(g415)
    c: Horizontal(g416)
    c: Vertical(g417)
    c: Horizontal(g418)
    c: Vertical(g419)
    c: Vertical(g421)
    c: Vertical(g423)
    c: Vertical(g425)
    c: Vertical(g427)
    c: Vertical(g429)
    c: Horizontal(g420)
    c: Horizontal(g422)
    c: Horizontal(g424)
    c: Vertical(g431)
    c: Vertical(g433)
    c: Vertical(g435)
    c: Horizontal(g436)
    c: Horizontal(g438)
    c: Vertical(g437)
    c: Coincident(g439,g505)
    c: Horizontal(g505)
    c: Coincident(g505,g506)
    c: Coincident(g506,g438)
    c: Vertical(g506)
    c: Horizontal(g464)
    c: Horizontal(g462)
    c: Horizontal(g460)
    c: Horizontal(g458)
    c: Horizontal(g456)
    c: Horizontal(g454)
    c: Horizontal(g452)
    c: Horizontal(g450)
    c: Horizontal(g448)
    c: Horizontal(g446)
    c: Horizontal(g444)
    c: Horizontal(g442)
    c: Horizontal(g440)
    c: Horizontal(g468)
    c: Horizontal(g470)
    c: Horizontal(g474)
    c: Horizontal(g476)
    c: Horizontal(g478)
    c: Vertical(g465)
    c: Horizontal(g466)
    c: Vertical(g475)
    c: Vertical(g477)
    c: Horizontal(g491)
    c: Horizontal(g496)
    c: Horizontal(g494)
    c: Horizontal(g498)
    c: Vertical(g499)
    c: Vertical(g497)
    c: Vertical(g495)
    c: Vertical(g493)
    c: Horizontal(g500)
    c: Horizontal(g502)
    c: Horizontal(g504)
    c: Vertical(g501)
    c: Vertical(g503)
    c: Coincident(g504,g507)
    c: Vertical(g507)
    c: Coincident(g507,g508)
    c: Coincident(g508,g509)
    c: Coincident(g509,g510)
    c: Coincident(g510,g511)
    c: Vertical(g511)
    c: Coincident(g511,g512)
    c: Horizontal(g512)
    c: Coincident(g512,g513)
    c: Vertical(g513)
    c: Coincident(g513,g514)
    c: Coincident(g514,g515)
    c: Vertical(g515)
    c: Coincident(g515,g516)
    c: Horizontal(g516)
    c: Coincident(g516,g517)
    c: Coincident(g517,g518)
    c: Horizontal(g518)
    c: Coincident(g518,g519)
    c: Coincident(g519,g520)
    c: Coincident(g521,g522)
    c: Coincident(g522,g523)
    c: Coincident(g523,g524)
    c: Coincident(g524,g525)
    c: Coincident(g525,g526)
    c: Coincident(g526,g527)
    c: Coincident(g527,g528)
    c: Coincident(g528,g529)
    c: Coincident(g529,g530)
    c: Coincident(g531,g532)
    c: Coincident(g532,g533)
    c: Coincident(g533,g534)
    c: Coincident(g534,g535)
    c: Coincident(g535,g536)
    c: Coincident(g536,g537)
    c: Coincident(g537,g538)
    c: Coincident(g538,g539)
    c: Coincident(g539,g540)
    c: Coincident(g540,g541)
    c: Coincident(g541,g542)
    c: Coincident(g542,g543)
    c: Coincident(g543,g544)
    c: Coincident(g544,g545)
    c: Coincident(g545,g546)
    c: Coincident(g546,g547)
    c: Coincident(g547,g548)
    c: Coincident(g548,g549)
    c: Coincident(g549,g550)
    c: Horizontal(g550)
    c: Coincident(g550,g551)
    c: Coincident(g551,g552)
    c: Coincident(g552,g553)
    c: Coincident(g553,g554)
    c: Horizontal(g554)
    c: Coincident(g554,g555)
    c: Coincident(g555,g556)
    c: Coincident(g556,g557)
    c: Coincident(g557,g558)
    c: Horizontal(g558)
    c: Coincident(g558,g559)
    c: Coincident(g559,g560)
    c: Coincident(g560,g561)
    c: Coincident(g562,g563)
    c: Horizontal(g563)
    c: Coincident(g563,g564)
    c: Coincident(g564,g565)
    c: Coincident(g565,g566)
    c: Coincident(g566,g567)
    c: Horizontal(g567)
    c: Coincident(g567,g568)
    c: Coincident(g568,g569)
    c: Coincident(g569,g570)
    c: Coincident(g570,g571)
    c: Coincident(g571,g572)
    c: Coincident(g572,g573)
    c: Coincident(g573,g574)
    c: Coincident(g574,g575)
    c: Coincident(g575,g576)
    c: Coincident(g576,g577)
    c: Coincident(g577,g578)
    c: Coincident(g578,g579)
    c: Coincident(g579,g580)
    c: Vertical(g580)
    c: Coincident(g580,g581)
    c: Coincident(g581,g582)
    c: Coincident(g582,g583)
    c: Coincident(g583,g584)
    c: Coincident(g584,g585)
    c: Horizontal(g585)
    c: Coincident(g585,g586)
    c: Coincident(g586,g587)
    c: Coincident(g587,g588)
    c: Vertical(g588)
    c: Coincident(g588,g589)
    c: Coincident(g589,g590)
    c: Coincident(g590,g591)
    c: Coincident(g592,g593)
    c: Horizontal(g593)
    c: Coincident(g593,g594)
    c: Coincident(g594,g595)
    c: Coincident(g595,g596)
    c: Vertical(g596)
    c: Coincident(g596,g597)
    c: Horizontal(g597)
    c: Coincident(g597,g598)
    c: Vertical(g598)
    c: Coincident(g598,g599)
    c: Coincident(g599,g600)
    c: Coincident(g600,g601)
    c: Horizontal(g601)
    c: Coincident(g601,g602)
    c: Coincident(g602,g603)
    c: Coincident(g603,g604)
    c: Coincident(g604,g605)
    c: Coincident(g605,g606)
    c: Coincident(g606,g607)
    c: Coincident(g607,g608)
    c: Coincident(g608,g609)
    c: Horizontal(g609)
    c: Coincident(g609,g610)
    c: Coincident(g610,g611)
    c: Coincident(g611,g612)
    c: Coincident(g612,g613)
    c: Vertical(g613)
    c: Coincident(g613,g614)
    c: Coincident(g614,g615)
    c: Vertical(g615)
    c: Coincident(g615,g616)
    c: Coincident(g616,g617)
    c: Vertical(g617)
    c: Coincident(g618,g619)
    c: Vertical(g619)
    c: Coincident(g619,g620)
    c: Coincident(g620,g621)
    c: Coincident(g621,g622)
    c: Coincident(g622,g623)
    c: Coincident(g623,g624)
    c: Coincident(g624,g625)
    c: Coincident(g625,g626)
    c: Coincident(g626,g627)
    c: Vertical(g627)
    c: Coincident(g627,g628)
    c: Coincident(g628,g629)
    c: Coincident(g629,g630)
    c: Coincident(g630,g631)
    c: Coincident(g631,g632)
    c: Coincident(g632,g633)
    c: Vertical(g633)
    c: Coincident(g633,g634)
    c: Coincident(g634,g635)
    c: Vertical(g635)
    c: Coincident(g635,g636)
    c: Coincident(g636,g637)
    c: Coincident(g637,g638)
    c: Coincident(g638,g639)
    c: Coincident(g639,g640)
    c: Horizontal(g640)
    c: Coincident(g640,g641)
    c: Coincident(g641,g642)
    c: Vertical(g642)
    c: Coincident(g642,g643)
    c: Coincident(g643,g644)
    c: Vertical(g644)
    c: Coincident(g644,g645)
    c: Coincident(g645,g646)
    c: Coincident(g646,g647)
    c: Coincident(g647,g648)
    c: Coincident(g648,g649)
    c: Coincident(g649,g650)
    c: Coincident(g650,g651)
    c: Coincident(g651,g652)
    c: Vertical(g652)
    c: Coincident(g652,g653)
    c: Coincident(g653,g654)
    c: Coincident(g654,g655)
    c: Coincident(g655,g656)
    c: Coincident(g656,g657)
    c: Coincident(g657,g658)
    c: Vertical(g658)
    c: Coincident(g658,g659)
    c: Coincident(g659,g660)
    c: Vertical(g660)
    c: Coincident(g660,g661)
    c: Coincident(g661,g662)
    c: Coincident(g662,g663)
    c: Coincident(g663,g664)
    c: Coincident(g664,g665)
    c: Coincident(g665,g666)
    c: Coincident(g666,g667)
    c: Coincident(g667,g668)
    c: Coincident(g668,g669)
    c: Coincident(g669,g670)
    c: Coincident(g670,g671)
    c: Coincident(g671,g672)
    c: Coincident(g672,g673)
    c: Horizontal(g673)
    c: Coincident(g673,g674)
    c: Coincident(g674,g675)
    c: Coincident(g675,g676)
    c: Coincident(g676,g677)
    c: Coincident(g677,g678)
    c: Vertical(g678)
    c: Coincident(g678,g679)
    c: Coincident(g680,g681)
    c: Vertical(g681)
    c: Coincident(g681,g682)
    c: Horizontal(g682)
    c: Coincident(g682,g683)
    c: Coincident(g683,g684)
    c: Coincident(g684,g685)
    c: Coincident(g685,g686)
    c: Coincident(g686,g687)
    c: Vertical(g687)
    c: Coincident(g687,g688)
    c: Coincident(g688,g689)
    c: Coincident(g689,g690)
    c: Coincident(g690,g691)
    c: Coincident(g691,g692)
    c: Coincident(g692,g693)
    c: Coincident(g693,g694)
    c: Horizontal(g694)
    c: Coincident(g694,g695)
    c: Horizontal(g508)
    c: Vertical(g509)
    c: Horizontal(g510)
    c: Vertical(g519)
    c: Vertical(g517)
    c: Horizontal(g520)
    c: Coincident(g520,g696)
    c: Coincident(g696,g697)
    c: Horizontal(g697)
    c: Coincident(g697,g698)
    c: Coincident(g698,g521)
    c: Vertical(g698)
    c: Vertical(g522)
    c: Vertical(g524)
    c: Vertical(g526)
    c: Horizontal(g523)
    c: Horizontal(g525)
    c: Horizontal(g527)
    c: Horizontal(g529)
    c: Horizontal(g532)
    c: Horizontal(g521)
    c: Vertical(g528)
    c: Vertical(g530)
    c: Coincident(g530,g699)
    c: Coincident(g699,g700)
    c: Coincident(g700,g701)
    c: Coincident(g701,g531)
    c: Vertical(g700)
    c: Vertical(g531)
    c: Vertical(g533)
    c: Vertical(g535)
    c: Vertical(g537)
    c: Vertical(g539)
    c: Vertical(g541)
    c: Horizontal(g534)
    c: Horizontal(g536)
    c: Horizontal(g538)
    c: Horizontal(g540)
    c: Horizontal(g542)
    c: Horizontal(g544)
    c: Horizontal(g546)
    c: Horizontal(g699)
    c: Horizontal(g701)
    c: Vertical(g543)
    c: Vertical(g545)
    c: Vertical(g547)
    c: Vertical(g549)
    c: Horizontal(g548)
    c: Vertical(g555)
    c: Vertical(g553)
    c: Vertical(g551)
    c: Horizontal(g552)
    c: Horizontal(g556)
    c: Horizontal(g560)
    c: Vertical(g557)
    c: Vertical(g559)
    c: Vertical(g561)
    c: Coincident(g702,g562)
    c: Coincident(g702,g561)
    c: Horizontal(g565)
    c: Horizontal(g569)
    c: Horizontal(g571)
    c: Horizontal(g573)
    c: Horizontal(g575)
    c: Horizontal(g702)
    c: Vertical(g566)
    c: Vertical(g568)
    c: Vertical(g570)
    c: Vertical(g572)
    c: Vertical(g574)
    c: Vertical(g576)
    c: Vertical(g578)
    c: Vertical(g582)
    c: Vertical(g584)
    c: Horizontal(g577)
    c: Horizontal(g579)
    c: Horizontal(g581)
    c: Horizontal(g583)
    c: Horizontal(g587)
    c: Horizontal(g589)
    c: Horizontal(g591)
    c: Coincident(g591,g592)
    c: Vertical(g590)
    c: Vertical(g592)
    c: Vertical(g594)
    c: Vertical(g602)
    c: Vertical(g604)
    c: Horizontal(g595)
    c: Horizontal(g599)
    c: Horizontal(g605)
    c: Horizontal(g607)
    c: Vertical(g608)
    c: Vertical(g611)
    c: Horizontal(g612)
    c: Horizontal(g614)
    c: Horizontal(g620)
    c: Horizontal(g622)
    c: Vertical(g621)
    c: Vertical(g623)
    c: Coincident(g618,g703)
    c: Vertical(g703)
    c: Coincident(g703,g704)
    c: Horizontal(g704)
    c: Coincident(g704,g617)
    c: Horizontal(g624)
    c: Vertical(g625)
    c: Horizontal(g643)
    c: Horizontal(g645)
    c: Horizontal(g647)
    c: Horizontal(g649)
    c: Horizontal(g651)
    c: Horizontal(g653)
    c: Horizontal(g655)
    c: Horizontal(g657)
    c: Horizontal(g659)
    c: Vertical(g656)
    c: Vertical(g654)
    c: Vertical(g650)
    c: Vertical(g648)
    c: Vertical(g646)
    c: Vertical(g637)
    c: Vertical(g639)
    c: Horizontal(g661)
    c: Horizontal(g663)
    c: Horizontal(g665)
    c: Horizontal(g667)
    c: Horizontal(g669)
    c: Horizontal(g671)
    c: Horizontal(g675)
    c: Vertical(g662)
    c: Vertical(g664)
    c: Vertical(g666)
    c: Vertical(g668)
    c: Vertical(g670)
    c: Vertical(g672)
    c: Vertical(g674)
    c: Vertical(g676)
    c: Horizontal(g677)
    c: Horizontal(g679)
    c: Coincident(g679,g705)
    c: Vertical(g705)
    c: Coincident(g705,g706)
    c: Horizontal(g706)
    c: Coincident(g706,g707)
    c: Coincident(g680,g707)
    c: Horizontal(g680)
    c: Vertical(g707)
    c: Vertical(g691)
    c: Vertical(g693)
    c: Vertical(g689)
    c: Vertical(g685)
    c: Vertical(g683)
    c: Horizontal(g686)
    c: Horizontal(g688)
    c: Horizontal(g690)
    c: Horizontal(g692)
    c: Horizontal(g684)
    c: Vertical(g695)
    c: Coincident(g695,g708)
    c: Coincident(g708,g709)
    c: Coincident(g709,g710)
    c: Coincident(g710,g711)
    c: Coincident(g711,g712)
    c: Coincident(g712,g713)
    c: Horizontal(g713)
    c: Coincident(g713,g714)
    c: Coincident(g714,g715)
    c: Coincident(g715,g716)
    c: Coincident(g716,g717)
    c: Coincident(g718,g719)
    c: Horizontal(g720)
    c: Coincident(g721,g722)
    c: Coincident(g722,g723)
    c: Coincident(g723,g724)
    c: Horizontal(g724)
    c: Coincident(g724,g725)
    c: Horizontal(g726)
    c: Coincident(g726,g727)
    c: Coincident(g727,g728)
    c: Horizontal(g728)
    c: Coincident(g728,g729)
    c: Coincident(g729,g730)
    c: Coincident(g730,g731)
    c: Coincident(g731,g732)
    c: Coincident(g732,g733)
    c: Coincident(g733,g734)
    c: Coincident(g734,g735)
    c: Coincident(g735,g736)
    c: Coincident(g736,g737)
    c: Coincident(g737,g738)
    c: Coincident(g738,g739)
    c: Coincident(g739,g740)
    c: Coincident(g740,g741)
    c: Coincident(g741,g742)
    c: Coincident(g742,g743)
    c: Coincident(g743,g744)
    c: Coincident(g744,g745)
    c: Coincident(g745,g746)
    c: Coincident(g746,g747)
    c: Coincident(g747,g748)
    c: Coincident(g748,g749)
    c: Coincident(g749,g750)
    c: Coincident(g750,g751)
    c: Coincident(g751,g752)
    c: Coincident(g752,g753)
    c: Coincident(g753,g754)
    c: Coincident(g754,g755)
    c: Coincident(g755,g756)
    c: Coincident(g756,g757)
    c: Coincident(g757,g758)
    c: Coincident(g760,g761)
    c: Coincident(g761,g762)
    c: Coincident(g762,g763)
    c: Coincident(g763,g764)
    c: Coincident(g765,g766)
    c: Coincident(g766,g767)
    c: Coincident(g767,g768)
    c: Coincident(g769,g770)
    c: Coincident(g770,g771)
    c: Coincident(g772,g773)
    c: Coincident(g773,g774)
    c: Coincident(g774,g775)
    c: Coincident(g775,g776)
    c: Coincident(g776,g777)
    c: Coincident(g777,g778)
    c: Coincident(g778,g779)
    c: Coincident(g779,g780)
    c: Coincident(g780,g781)
    c: Coincident(g781,g782)
    c: Coincident(g782,g783)
    c: Coincident(g783,g784)
    c: Coincident(g784,g785)
    c: Coincident(g785,g786)
    c: Horizontal(g787)
    c: Coincident(g787,g788)
    c: Coincident(g788,g789)
    c: Coincident(g789,g790)
    c: Coincident(g790,g791)
    c: Horizontal(g791)
    c: Coincident(g791,g792)
    c: Coincident(g792,g793)
    c: Horizontal(g793)
    c: Coincident(g793,g794)
    c: Coincident(g794,g795)
    c: Coincident(g795,g796)
    c: Vertical(g796)
    c: Coincident(g796,g797)
    c: Horizontal(g797)
    c: Coincident(g797,g798)
    c: Coincident(g798,g799)
    c: Horizontal(g799)
    c: Coincident(g799,g800)
    c: Coincident(g800,g801)
    c: Coincident(g801,g802)
    c: Coincident(g802,g803)
    c: Horizontal(g803)
    c: Vertical(g804)
    c: Coincident(g804,g805)
    c: Coincident(g805,g806)
    c: Coincident(g806,g807)
    c: Coincident(g807,g808)
    c: Coincident(g808,g809)
    c: Coincident(g809,g810)
    c: Vertical(g810)
    c: Coincident(g810,g811)
    c: Coincident(g811,g812)
    c: Coincident(g812,g813)
    c: Coincident(g813,g814)
    c: Coincident(g814,g815)
    c: Horizontal(g815)
    c: Coincident(g815,g816)
    c: Coincident(g816,g817)
    c: Coincident(g817,g818)
    c: Coincident(g818,g819)
    c: Coincident(g819,g820)
    c: Coincident(g820,g821)
    c: Horizontal(g821)
    c: Coincident(g821,g822)
    c: Vertical(g822)
    c: Coincident(g822,g823)
    c: Coincident(g823,g824)
    c: Coincident(g824,g825)
    c: Horizontal(g825)
    c: Coincident(g825,g826)
    c: Coincident(g826,g827)
    c: Coincident(g827,g828)
    c: Coincident(g828,g829)
    c: Horizontal(g829)
    c: Coincident(g829,g830)
    c: Coincident(g830,g831)
    c: Coincident(g831,g832)
    c: Coincident(g832,g833)
    c: Horizontal(g834)
    c: Coincident(g834,g835)
    c: Coincident(g835,g836)
    c: Horizontal(g836)
    c: Coincident(g836,g837)
    c: Coincident(g837,g838)
    c: Horizontal(g838)
    c: Coincident(g838,g839)
    c: Coincident(g839,g840)
    c: Coincident(g840,g841)
    c: Coincident(g841,g842)
    c: Coincident(g842,g843)
    c: Coincident(g843,g844)
    c: Coincident(g844,g845)
    c: Coincident(g845,g846)
    c: Coincident(g846,g847)
    c: Coincident(g847,g848)
    c: Horizontal(g848)
    c: Coincident(g848,g849)
    c: Coincident(g849,g850)
    c: Coincident(g850,g851)
    c: Coincident(g851,g852)
    c: Coincident(g852,g853)
    c: Coincident(g853,g854)
    c: Coincident(g854,g855)
    c: Coincident(g855,g856)
    c: Coincident(g856,g857)
    c: Coincident(g857,g858)
    c: Horizontal(g858)
    c: Coincident(g858,g859)
    c: Coincident(g859,g860)
    c: Coincident(g860,g861)
    c: Coincident(g861,g862)
    c: Coincident(g862,g863)
    c: Coincident(g863,g864)
    c: Coincident(g786,g865)
    c: Coincident(g865,g866)
    c: Coincident(g866,g787)
    c: Vertical(g866)
    c: Horizontal(g709)
    c: Horizontal(g711)
    c: Horizontal(g715)
    c: Horizontal(g717)
    c: Horizontal(g719)
    c: Horizontal(g722)
    c: Coincident(g718,g867)
    c: Horizontal(g867)
    c: Coincident(g867,g868)
    c: Coincident(g868,g717)
    c: Coincident(g721,g869)
    c: Coincident(g869,g870)
    c: Coincident(g720,g870)
    c: Coincident(g871,g720)
    c: Coincident(g871,g719)
    c: Vertical(g871)
    c: Vertical(g870)
    c: Vertical(g723)
    c: Horizontal(g869)
    c: Coincident(g872,g726)
    c: Coincident(g873,g872)
    c: Coincident(g725,g873)
    c: Horizontal(g873)
    c: Horizontal(g736)
    c: Horizontal(g734)
    c: Horizontal(g732)
    c: Horizontal(g730)
    c: Horizontal(g738)
    c: Horizontal(g740)
    c: Horizontal(g742)
    c: Horizontal(g744)
    c: Horizontal(g746)
    c: Horizontal(g748)
    c: Horizontal(g750)
    c: Horizontal(g752)
    c: Horizontal(g754)
    c: Coincident(g758,g759)
    c: Horizontal(g756)
    c: Horizontal(g758)
    c: Coincident(g874,g759)
    c: Horizontal(g874)
    c: Coincident(g875,g760)
    c: Coincident(g875,g874)
    c: Horizontal(g760)
    c: Vertical(g762)
    c: Coincident(g765,g764)
    c: Vertical(g764)
    c: Vertical(g766)
    c: Vertical(g768)
    c: Coincident(g769,g768)
    c: Vertical(g770)
    c: Coincident(g876,g771)
    c: Coincident(g877,g772)
    c: Coincident(g877,g876)
    c: Vertical(g772)
    c: Vertical(g774)
    c: Vertical(g776)
    c: Vertical(g778)
    c: Vertical(g780)
    c: Vertical(g782)
    c: Vertical(g876)
    c: Horizontal(g773)
    c: Horizontal(g775)
    c: Horizontal(g777)
    c: Horizontal(g779)
    c: Horizontal(g781)
    c: Horizontal(g783)
    c: Horizontal(g785)
    c: Horizontal(g865)
    c: Vertical(g784)
    c: Vertical(g786)
    c: Vertical(g788)
    c: Vertical(g790)
    c: Horizontal(g789)
    c: Vertical(g792)
    c: Vertical(g794)
    c: Horizontal(g795)
    c: Vertical(g798)
    c: Vertical(g800)
    c: Vertical(g802)
    c: Horizontal(g801)
    c: Coincident(g804,g803)
    c: Horizontal(g805)
    c: Horizontal(g807)
    c: Horizontal(g809)
    c: Vertical(g806)
    c: Vertical(g808)
    c: Vertical(g812)
    c: Vertical(g816)
    c: Vertical(g814)
    c: Vertical(g818)
    c: Vertical(g820)
    c: Vertical(g824)
    c: Vertical(g826)
    c: Vertical(g828)
    c: Vertical(g830)
    c: Vertical(g832)
    c: Horizontal(g827)
    c: Horizontal(g823)
    c: Horizontal(g819)
    c: Horizontal(g817)
    c: Horizontal(g831)
    c: Horizontal(g833)
    c: Coincident(g878,g833)
    c: Coincident(g878,g834)
    c: Vertical(g837)
    c: Horizontal(g840)
    c: Horizontal(g842)
    c: Horizontal(g846)
    c: Horizontal(g850)
    c: Horizontal(g852)
    c: Horizontal(g854)
    c: Horizontal(g856)
    c: Horizontal(g860)
    c: Horizontal(g862)
    c: Horizontal(g864)
    c: Horizontal(g844)
    c: Coincident(g864,g879)
    c: Coincident(g879,g880)
    c: Coincident(g880,g881)
    c: Coincident(g881,g882)
    c: Horizontal(g882)
    c: Coincident(g883,g1)
    c: Coincident(g883,g0)
    c: Vertical(g883)
    c: Coincident(g0,g882)
    c: Coincident(g1,g2)
    c: Coincident(g3,g4)
    c: Coincident(g4,g5)
    c: Coincident(g5,g6)
    c: Coincident(g6,g7)
    c: Coincident(g13,g14)
    c: Coincident(g14,g15)
    c: Coincident(g16,g17)
    c: Coincident(g18,g19)
    c: Coincident(g22,g23)
    c: Coincident(g24,g25)
    c: Coincident(g27,g28)
    c: Vertical(g26)
    c: Coincident(g28,g29)
    c: Coincident(g30,g31)
    c: Horizontal(g29)
    c: Coincident(g37,g38)
    c: Coincident(g38,g39)
    c: Coincident(g39,g40)
    c: Coincident(g40,g41)
    c: Coincident(g42,g43)
    c: Coincident(g20,g21)
    c: Coincident(g21,g22)
    c: Coincident(g25,g26)
    c: Coincident(g48,g49)
    c: Coincident(g49,g50)
    c: Coincident(g58,g59)
    c: Horizontal(g59)
    c: Coincident(g61,g62)
    c: Coincident(g64,g65)
    c: Coincident(g65,g66)
    c: Coincident(g66,g67)
    c: Coincident(g68,g69)
    c: Coincident(g70,g71)
    c: Coincident(g72,g73)
    c: Coincident(g74,g75)
    c: Coincident(g86,g87)
    c: Coincident(g87,g88)
    c: Coincident(g92,g93)
    c: Coincident(g94,g95)
    c: Coincident(g96,g97)
    c: Coincident(g51,g52)
    c: Coincident(g62,g63)
    c: Coincident(g76,g77)
    c: Coincident(g77,g78)
    c: Coincident(g82,g83)
    c: Coincident(g83,g84)
FEATURE [Mesh::Feature] tinker
  Placement = pos=(42,-32.19,20) rot=(1,0,0;1.5708rad)
FEATURE [Part::Extrusion] Extrude
  Base = -> Sketch013
  Dir = (0,1,0)
  DirMode = 0
  FaceMakerClass = Part::FaceMakerBullseye
  LengthFwd = 10
  LengthRev = 0
  Solid = true
  Symmetric = false
FEATURE [Part::FeaturePython] Clone  label="scaled0_75"  # Draft clone (typed FeaturePython)
  AttacherType = Attacher::AttachEngine3D
  Fuse = false
  Objects = -> [Extrude]
  Scale = (0.75,0.75,0.75)
FEATURE [Part::FeaturePython] Clone001  label="scaled0_85"  # Draft clone (typed FeaturePython)
  AttacherType = Attacher::AttachEngine3D
  Fuse = false
  Objects = -> [Extrude]
  Scale = (0.8,0.8,0.8)
